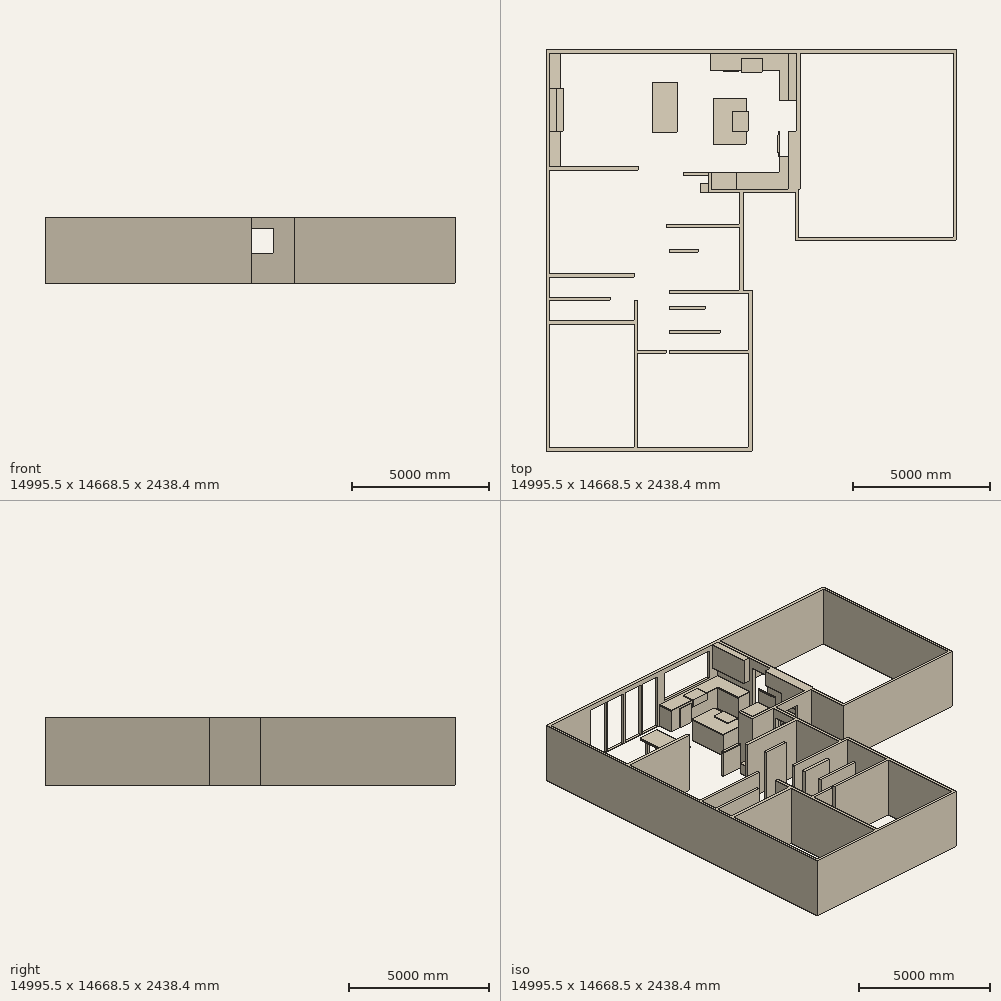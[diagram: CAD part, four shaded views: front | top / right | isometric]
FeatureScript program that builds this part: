
annotation { "Feature Type Name" : "Feature", "Feature Type Description" : "" }
export const myFeature = defineFeature(function(context is Context, id is Id, definition is map)
    precondition{}
    {
        {
            var Q0;
            Q0=qCreatedBy(makeId("Top.planeOp"),FACE);
            var sketch = newSketch(context, id + "F0", { "sketchPlane" : qUnion([Q0])});
            skLineSegment(sketch, "E0.bottom", {"start": v(9277.35, -5108.57) * mm, "end": v(9156.7, -5108.57) * mm});
            skLineSegment(sketch, "E0.top", {"start": v(9277.35, -120.65) * mm, "end": v(9156.7, -120.65) * mm});
            skLineSegment(sketch, "E0.left", {"start": v(9277.35, -5108.57) * mm, "end": v(9277.35, -120.65) * mm});
            skLineSegment(sketch, "E0.right", {"start": v(9156.7, -5108.57) * mm, "end": v(9156.7, -120.65) * mm});
            skLineSegment(sketch, "E1.bottom", {"start": v(7067.55, -5108.57) * mm, "end": v(4381.5, -5108.57) * mm});
            skLineSegment(sketch, "E1.top", {"start": v(7067.55, -5229.22) * mm, "end": v(4381.5, -5229.23) * mm});
            skLineSegment(sketch, "E1.left", {"start": v(7067.55, -5108.57) * mm, "end": v(7067.55, -5229.22) * mm});
            skLineSegment(sketch, "E1.right", {"start": v(4381.5, -5108.57) * mm, "end": v(4381.5, -5229.23) * mm});
            skLineSegment(sketch, "E2.bottom", {"start": v(5921.37, -5108.57) * mm, "end": v(6042.03, -5108.57) * mm});
            skLineSegment(sketch, "E2.top", {"start": v(5921.37, -1587.5) * mm, "end": v(6042.03, -1587.5) * mm});
            skLineSegment(sketch, "E2.left", {"start": v(5921.38, -5108.57) * mm, "end": v(5921.37, -1587.5) * mm});
            skLineSegment(sketch, "E2.right", {"start": v(6042.03, -5108.57) * mm, "end": v(6042.02, -1587.5) * mm});
            skLineSegment(sketch, "E3.bottom", {"start": v(4381.5, -5108.57) * mm, "end": v(4502.15, -5108.57) * mm});
            skLineSegment(sketch, "E3.top", {"start": v(4381.5, -4279.9) * mm, "end": v(4502.15, -4279.9) * mm});
            skLineSegment(sketch, "E3.left", {"start": v(4381.5, -5108.57) * mm, "end": v(4381.5, -4279.9) * mm});
            skLineSegment(sketch, "E3.right", {"start": v(4502.15, -5108.57) * mm, "end": v(4502.15, -4279.9) * mm});
            skLineSegment(sketch, "E4.bottom", {"start": v(4502.15, -4279.9) * mm, "end": v(5921.37, -4279.9) * mm});
            skLineSegment(sketch, "E4.top", {"start": v(4502.15, -4400.55) * mm, "end": v(5921.38, -4400.55) * mm});
            skLineSegment(sketch, "E4.left", {"start": v(4502.15, -4279.9) * mm, "end": v(4502.15, -4400.55) * mm});
            skLineSegment(sketch, "E4.right", {"start": v(5921.38, -4279.9) * mm, "end": v(5921.38, -4400.55) * mm});
            skLineSegment(sketch, "E5.bottom", {"start": v(120.65, -4279.9) * mm, "end": v(3346.45, -4279.9) * mm});
            skLineSegment(sketch, "E5.top", {"start": v(120.65, -4400.55) * mm, "end": v(3346.45, -4400.55) * mm});
            skLineSegment(sketch, "E5.left", {"start": v(120.65, -4279.9) * mm, "end": v(120.65, -4400.55) * mm});
            skLineSegment(sketch, "E5.right", {"start": v(3346.45, -4279.9) * mm, "end": v(3346.45, -4400.55) * mm});
            skLineSegment(sketch, "E6.bottom", {"start": v(3346.45, -4400.55) * mm, "end": v(3225.8, -4400.55) * mm});
            skLineSegment(sketch, "E6.top", {"start": v(3346.45, -9169.4) * mm, "end": v(3225.8, -9169.4) * mm});
            skLineSegment(sketch, "E6.left", {"start": v(3346.45, -4400.55) * mm, "end": v(3346.45, -9169.4) * mm});
            skLineSegment(sketch, "E6.right", {"start": v(3225.8, -4400.55) * mm, "end": v(3225.8, -9169.4) * mm});
            skLineSegment(sketch, "E7.bottom", {"start": v(2343.15, -9169.4) * mm, "end": v(120.65, -9169.4) * mm});
            skLineSegment(sketch, "E7.top", {"start": v(2343.15, -9048.75) * mm, "end": v(120.65, -9048.75) * mm});
            skLineSegment(sketch, "E7.left", {"start": v(3225.8, -9169.4) * mm, "end": v(3225.8, -9048.75) * mm});
            skLineSegment(sketch, "E7.right", {"start": v(120.65, -9169.4) * mm, "end": v(120.65, -9048.75) * mm});
            skLineSegment(sketch, "E8.bottom", {"start": v(3225.8, -8191.5) * mm, "end": v(120.65, -8191.5) * mm});
            skLineSegment(sketch, "E8.top", {"start": v(3225.8, -8312.15) * mm, "end": v(120.65, -8312.15) * mm});
            skLineSegment(sketch, "E8.left", {"start": v(3225.8, -8191.5) * mm, "end": v(3225.8, -8312.15) * mm});
            skLineSegment(sketch, "E8.right", {"start": v(120.65, -8191.5) * mm, "end": v(120.65, -8312.15) * mm});
            skLineSegment(sketch, "E9.bottom", {"start": v(7067.55, -6486.53) * mm, "end": v(4381.5, -6486.53) * mm});
            skLineSegment(sketch, "E9.top", {"start": v(7067.55, -6365.87) * mm, "end": v(4381.5, -6365.88) * mm});
            skLineSegment(sketch, "E9.left", {"start": v(7067.55, -6486.53) * mm, "end": v(7067.55, -6365.87) * mm});
            skLineSegment(sketch, "E9.right", {"start": v(4381.5, -6486.53) * mm, "end": v(4381.5, -6365.88) * mm});
            skLineSegment(sketch, "E10.bottom", {"start": v(4381.5, -6486.53) * mm, "end": v(4502.15, -6486.53) * mm});
            skLineSegment(sketch, "E10.top", {"start": v(4381.5, -11118.85) * mm, "end": v(4502.15, -11118.85) * mm});
            skLineSegment(sketch, "E10.left", {"start": v(4381.5, -6486.53) * mm, "end": v(4381.5, -11118.85) * mm});
            skLineSegment(sketch, "E10.right", {"start": v(4502.15, -6486.53) * mm, "end": v(4502.15, -11118.85) * mm});
            skLineSegment(sketch, "E11.bottom", {"start": v(4502.15, -8791.57) * mm, "end": v(7067.55, -8791.57) * mm});
            skLineSegment(sketch, "E11.top", {"start": v(4502.15, -8912.22) * mm, "end": v(7067.55, -8912.22) * mm});
            skLineSegment(sketch, "E11.left", {"start": v(4502.15, -8791.57) * mm, "end": v(4502.15, -8912.22) * mm});
            skLineSegment(sketch, "E11.right", {"start": v(7067.55, -8791.57) * mm, "end": v(7067.55, -8912.22) * mm});
            skLineSegment(sketch, "E12.bottom", {"start": v(4502.15, -11118.85) * mm, "end": v(7397.75, -11118.85) * mm});
            skLineSegment(sketch, "E12.top", {"start": v(4502.15, -10998.2) * mm, "end": v(7397.75, -10998.2) * mm});
            skLineSegment(sketch, "E12.left", {"start": v(4502.15, -11118.85) * mm, "end": v(4502.15, -10998.2) * mm});
            skLineSegment(sketch, "E12.right", {"start": v(7397.75, -11118.85) * mm, "end": v(7397.75, -10998.2) * mm});
            skLineSegment(sketch, "E13.top", {"start": v(3346.45, -14547.85) * mm, "end": v(3225.8, -14547.85) * mm});
            skLineSegment(sketch, "E13.left", {"start": v(3346.45, -9169.4) * mm, "end": v(3346.45, -14547.85) * mm});
            skLineSegment(sketch, "E13.right", {"start": v(3225.8, -9169.4) * mm, "end": v(3225.8, -14547.85) * mm});
            skLineSegment(sketch, "E14.bottom", {"start": v(3225.8, -10026.65) * mm, "end": v(120.65, -10026.65) * mm});
            skLineSegment(sketch, "E14.top", {"start": v(3225.8, -9906) * mm, "end": v(120.65, -9906) * mm});
            skLineSegment(sketch, "E14.left", {"start": v(3225.8, -10026.65) * mm, "end": v(3225.8, -9906) * mm});
            skLineSegment(sketch, "E14.right", {"start": v(120.65, -10026.65) * mm, "end": v(120.65, -9906) * mm});
            skLineSegment(sketch, "E15.bottom", {"start": v(4381.5, -11118.85) * mm, "end": v(3346.45, -11118.85) * mm});
            skLineSegment(sketch, "E15.top", {"start": v(4381.5, -10998.2) * mm, "end": v(3346.45, -10998.2) * mm});
            skLineSegment(sketch, "E15.left", {"start": v(4381.5, -11118.85) * mm, "end": v(4381.5, -10998.2) * mm});
            skLineSegment(sketch, "E15.right", {"start": v(3346.45, -11118.85) * mm, "end": v(3346.45, -10998.2) * mm});
            skLineSegment(sketch, "E16.bottom", {"start": v(4502.15, -10363.2) * mm, "end": v(6369.05, -10363.2) * mm});
            skLineSegment(sketch, "E16.top", {"start": v(4502.15, -10242.55) * mm, "end": v(6369.05, -10242.55) * mm});
            skLineSegment(sketch, "E16.left", {"start": v(4502.15, -10363.2) * mm, "end": v(4502.15, -10242.55) * mm});
            skLineSegment(sketch, "E16.right", {"start": v(6369.05, -10363.2) * mm, "end": v(6369.05, -10242.55) * mm});
            skLineSegment(sketch, "E17.bottom", {"start": v(6369.05, -10363.2) * mm, "end": v(6248.4, -10363.2) * mm});
            skLineSegment(sketch, "E17.top", {"start": v(6369.05, -10998.2) * mm, "end": v(6248.4, -10998.2) * mm});
            skLineSegment(sketch, "E17.left", {"start": v(6369.05, -10363.2) * mm, "end": v(6369.05, -10998.2) * mm});
            skLineSegment(sketch, "E17.right", {"start": v(6248.4, -10363.2) * mm, "end": v(6248.4, -10998.2) * mm});
            skLineSegment(sketch, "E18.bottom", {"start": v(2343.15, -8312.15) * mm, "end": v(2463.8, -8312.15) * mm});
            skLineSegment(sketch, "E18.top", {"start": v(2343.15, -9906) * mm, "end": v(2463.8, -9906) * mm});
            skLineSegment(sketch, "E18.left", {"start": v(2343.15, -8312.15) * mm, "end": v(2343.15, -9906) * mm});
            skLineSegment(sketch, "E18.right", {"start": v(2463.8, -8312.15) * mm, "end": v(2463.8, -9906) * mm});
            skLineSegment(sketch, "E19.bottom", {"start": v(4502.15, -7419.98) * mm, "end": v(5562.6, -7419.98) * mm});
            skLineSegment(sketch, "E19.top", {"start": v(4502.15, -7299.33) * mm, "end": v(5562.6, -7299.33) * mm});
            skLineSegment(sketch, "E19.left", {"start": v(4502.15, -7419.98) * mm, "end": v(4502.15, -7299.33) * mm});
            skLineSegment(sketch, "E19.right", {"start": v(5562.6, -7419.98) * mm, "end": v(5562.6, -7299.33) * mm});
            skLineSegment(sketch, "E20.bottom", {"start": v(5562.6, -7299.33) * mm, "end": v(5441.95, -7299.33) * mm});
            skLineSegment(sketch, "E20.top", {"start": v(5562.6, -6486.53) * mm, "end": v(5441.95, -6486.53) * mm});
            skLineSegment(sketch, "E20.left", {"start": v(5562.6, -7299.33) * mm, "end": v(5562.6, -6486.53) * mm});
            skLineSegment(sketch, "E20.right", {"start": v(5441.95, -7299.33) * mm, "end": v(5441.95, -6486.53) * mm});
            skLineSegment(sketch, "E21.bottom", {"start": v(4502.15, -9369.42) * mm, "end": v(5816.6, -9369.42) * mm});
            skLineSegment(sketch, "E21.top", {"start": v(4502.15, -9490.07) * mm, "end": v(5816.6, -9490.07) * mm});
            skLineSegment(sketch, "E21.left", {"start": v(4502.15, -9369.42) * mm, "end": v(4502.15, -9490.07) * mm});
            skLineSegment(sketch, "E21.right", {"start": v(5816.6, -9369.42) * mm, "end": v(5816.6, -9490.07) * mm});
            skLineSegment(sketch, "E22.bottom", {"start": v(5816.6, -9369.42) * mm, "end": v(5695.95, -9369.42) * mm});
            skLineSegment(sketch, "E22.top", {"start": v(5816.6, -8912.22) * mm, "end": v(5695.95, -8912.22) * mm});
            skLineSegment(sketch, "E22.left", {"start": v(5816.6, -9369.42) * mm, "end": v(5816.6, -8912.22) * mm});
            skLineSegment(sketch, "E22.right", {"start": v(5695.95, -9369.42) * mm, "end": v(5695.95, -8912.22) * mm});
            skLineSegment(sketch, "E23", {"start": v(0, 0) * mm, "end": v(0, -14668.5) * mm});
            skLineSegment(sketch, "E24", {"start": v(0, -14668.5) * mm, "end": v(7518.4, -14668.5) * mm});
            skLineSegment(sketch, "E25", {"start": v(7518.4, -14668.5) * mm, "end": v(7518.4, -8791.57) * mm});
            skLineSegment(sketch, "E26", {"start": v(7188.2, -8791.57) * mm, "end": v(7518.4, -8791.57) * mm});
            skLineSegment(sketch, "E27", {"start": v(7188.2, -8791.57) * mm, "end": v(7188.2, -5229.22) * mm});
            skLineSegment(sketch, "E28", {"start": v(7188.2, -5229.22) * mm, "end": v(9099.55, -5229.22) * mm});
            skLineSegment(sketch, "E29", {"start": v(9099.55, -5229.22) * mm, "end": v(9099.55, -6985) * mm});
            skLineSegment(sketch, "E30", {"start": v(9099.55, -6985) * mm, "end": v(14995.53, -6985) * mm});
            skLineSegment(sketch, "E31", {"start": v(14995.53, -6985) * mm, "end": v(14995.53, 0) * mm});
            skLineSegment(sketch, "E32", {"start": v(14995.53, 0) * mm, "end": v(0, 0) * mm});
            skLineSegment(sketch, "E33.0", {"start": v(14874.88, -6864.35) * mm, "end": v(14874.88, -120.65) * mm});
            skLineSegment(sketch, "E33.1", {"start": v(9220.2, -6864.35) * mm, "end": v(14874.88, -6864.35) * mm});
            skLineSegment(sketch, "E33.2", {"start": v(14874.88, -120.65) * mm, "end": v(120.65, -120.65) * mm});
            skLineSegment(sketch, "E33.3", {"start": v(9220.2, -5108.57) * mm, "end": v(9220.2, -6864.35) * mm});
            skLineSegment(sketch, "E33.4", {"start": v(7067.55, -5108.57) * mm, "end": v(9220.2, -5108.57) * mm});
            skLineSegment(sketch, "E33.5", {"start": v(7067.55, -8912.22) * mm, "end": v(7067.55, -5108.57) * mm});
            skLineSegment(sketch, "E33.6", {"start": v(120.65, -120.65) * mm, "end": v(120.65, -14547.85) * mm});
            skLineSegment(sketch, "E33.7", {"start": v(120.65, -14547.85) * mm, "end": v(7397.75, -14547.85) * mm});
            skLineSegment(sketch, "E33.8", {"start": v(7397.75, -14547.85) * mm, "end": v(7397.75, -8912.22) * mm});
            skLineSegment(sketch, "E34", {"start": v(7397.75, -8912.22) * mm, "end": v(7067.55, -8912.22) * mm});
            skLineSegment(sketch, "E35", {"start": v(5921.38, -2908.3) * mm, "end": v(6042.03, -2908.3) * mm});
            skSolve(sketch);
        }
        {
            var Q0;
            Q0=makeQuery(id+"F0.imprint","IMPRINT",FACE,{"disambiguationData":[TD([[makeQuery(id+"F0.imprint","IMPRINT",EDGE,{"derivedFrom":sQuery(id+"F0.wireOp",EDGE,"E23")}),1.0]])]});
            var Q1;
            {var subQ3=sQuery(id+"F0.wireOp",EDGE,"E0.bottom");Q1=makeQuery(id+"F0.imprint","IMPRINT",FACE,{"disambiguationData":[TD([[makeQuery(id+"F0.imprint","IMPRINT",EDGE,{"derivedFrom":subQ3}),-1.0]])]});}
            var Q2;
            {var subQ0=sQuery(id+"F0.wireOp",EDGE,"E1.top");Q2=makeQuery(id+"F0.imprint","IMPRINT",FACE,{"disambiguationData":[TD([[makeQuery(id+"F0.imprint","IMPRINT",EDGE,{"derivedFrom":subQ0}),-1.0]])]});}
            var Q3;
            Q3=makeQuery(id+"F0.imprint","IMPRINT",FACE,{"disambiguationData":[TD([[makeQuery(id+"F0.imprint","IMPRINT",EDGE,{"derivedFrom":sQuery(id+"F0.wireOp",EDGE,"E3.bottom")}),1.0]])]});
            var Q4;
            Q4=makeQuery(id+"F0.imprint","IMPRINT",FACE,{"disambiguationData":[TD([[makeQuery(id+"F0.imprint","IMPRINT",EDGE,{"derivedFrom":sQuery(id+"F0.wireOp",EDGE,"E4.bottom")}),-1.0]])]});
            var Q5;
            {var subQ3=sQuery(id+"F0.wireOp",EDGE,"E2.bottom");Q5=makeQuery(id+"F0.imprint","IMPRINT",FACE,{"disambiguationData":[TD([[makeQuery(id+"F0.imprint","IMPRINT",EDGE,{"derivedFrom":subQ3}),1.0]])]});}
            var Q6;
            {var subQ1=sQuery(id+"F0.wireOp",EDGE,"E5.bottom");Q6=makeQuery(id+"F0.imprint","IMPRINT",FACE,{"disambiguationData":[TD([[makeQuery(id+"F0.imprint","IMPRINT",EDGE,{"derivedFrom":subQ1}),-1.0]])]});}
            var Q7;
            {var subQ3=sQuery(id+"F0.wireOp",EDGE,"E6.bottom");Q7=makeQuery(id+"F0.imprint","IMPRINT",FACE,{"disambiguationData":[TD([[makeQuery(id+"F0.imprint","IMPRINT",EDGE,{"derivedFrom":subQ3}),1.0]])]});}
            var Q8;
            {var subQ5=sQuery(id+"F0.wireOp",EDGE,"E8.bottom");Q8=makeQuery(id+"F0.imprint","IMPRINT",FACE,{"disambiguationData":[TD([[makeQuery(id+"F0.imprint","IMPRINT",EDGE,{"derivedFrom":subQ5}),1.0]])]});}
            var Q9;
            {var subQ3=sQuery(id+"F0.wireOp",EDGE,"E18.bottom");Q9=makeQuery(id+"F0.imprint","IMPRINT",FACE,{"disambiguationData":[TD([[makeQuery(id+"F0.imprint","IMPRINT",EDGE,{"derivedFrom":subQ3}),-1.0]])]});}
            var Q10;
            {var subQ0=sQuery(id+"F0.wireOp",EDGE,"E7.bottom");Q10=makeQuery(id+"F0.imprint","IMPRINT",FACE,{"disambiguationData":[TD([[makeQuery(id+"F0.imprint","IMPRINT",EDGE,{"derivedFrom":subQ0}),-1.0]])]});}
            var Q11;
            {var subQ1=sQuery(id+"F0.wireOp",EDGE,"E6.top");Q11=makeQuery(id+"F0.imprint","IMPRINT",FACE,{"disambiguationData":[TD([[makeQuery(id+"F0.imprint","IMPRINT",EDGE,{"derivedFrom":subQ1}),1.0]])]});}
            var Q12;
            {var subQ5=sQuery(id+"F0.wireOp",EDGE,"E14.bottom");Q12=makeQuery(id+"F0.imprint","IMPRINT",FACE,{"disambiguationData":[TD([[makeQuery(id+"F0.imprint","IMPRINT",EDGE,{"derivedFrom":subQ5}),-1.0]])]});}
            var Q13;
            {var subQ6=sQuery(id+"F0.wireOp",EDGE,"E10.bottom");Q13=makeQuery(id+"F0.imprint","IMPRINT",FACE,{"disambiguationData":[TD([[makeQuery(id+"F0.imprint","IMPRINT",EDGE,{"derivedFrom":subQ6}),-1.0]])]});}
            var Q14;
            Q14=makeQuery(id+"F0.imprint","IMPRINT",FACE,{"disambiguationData":[TD([[makeQuery(id+"F0.imprint","IMPRINT",EDGE,{"derivedFrom":sQuery(id+"F0.wireOp",EDGE,"E21.bottom")}),-1.0]])]});
            var Q15;
            Q15=makeQuery(id+"F0.imprint","IMPRINT",FACE,{"disambiguationData":[TD([[makeQuery(id+"F0.imprint","IMPRINT",EDGE,{"derivedFrom":sQuery(id+"F0.wireOp",EDGE,"E16.bottom")}),1.0]])]});
            var Q16;
            {var subQ5=sQuery(id+"F0.wireOp",EDGE,"E11.bottom");Q16=makeQuery(id+"F0.imprint","IMPRINT",FACE,{"disambiguationData":[TD([[makeQuery(id+"F0.imprint","IMPRINT",EDGE,{"derivedFrom":subQ5}),-1.0]])]});}
            var Q17;
            Q17=makeQuery(id+"F0.imprint","IMPRINT",FACE,{"disambiguationData":[TD([[makeQuery(id+"F0.imprint","IMPRINT",EDGE,{"derivedFrom":sQuery(id+"F0.wireOp",EDGE,"E22.bottom")}),-1.0]])]});
            var Q18;
            Q18=makeQuery(id+"F0.imprint","IMPRINT",FACE,{"disambiguationData":[TD([[makeQuery(id+"F0.imprint","IMPRINT",EDGE,{"derivedFrom":sQuery(id+"F0.wireOp",EDGE,"E17.bottom")}),1.0]])]});
            var Q19;
            {var subQ1=sQuery(id+"F0.wireOp",EDGE,"E9.top");Q19=makeQuery(id+"F0.imprint","IMPRINT",FACE,{"disambiguationData":[TD([[makeQuery(id+"F0.imprint","IMPRINT",EDGE,{"derivedFrom":subQ1}),1.0]])]});}
            var Q20;
            Q20=makeQuery(id+"F0.imprint","IMPRINT",FACE,{"disambiguationData":[TD([[makeQuery(id+"F0.imprint","IMPRINT",EDGE,{"derivedFrom":sQuery(id+"F0.wireOp",EDGE,"E20.bottom")}),-1.0]])]});
            var Q21;
            Q21=makeQuery(id+"F0.imprint","IMPRINT",FACE,{"disambiguationData":[TD([[makeQuery(id+"F0.imprint","IMPRINT",EDGE,{"derivedFrom":sQuery(id+"F0.wireOp",EDGE,"E19.bottom")}),1.0]])]});
            var Q22;
            {var subQ5=sQuery(id+"F0.wireOp",EDGE,"E12.bottom");Q22=makeQuery(id+"F0.imprint","IMPRINT",FACE,{"disambiguationData":[TD([[makeQuery(id+"F0.imprint","IMPRINT",EDGE,{"derivedFrom":subQ5}),1.0]])]});}
            var Q23;
            Q23=makeQuery(id+"F0.imprint","IMPRINT",FACE,{"disambiguationData":[TD([[makeQuery(id+"F0.imprint","IMPRINT",EDGE,{"derivedFrom":sQuery(id+"F0.wireOp",EDGE,"E15.bottom")}),-1.0]])]});
            extrude(context, id + "F1", {"entities" : qUnion([Q0, Q1, Q2, Q3, Q4, Q5, Q6, Q7, Q8, Q9, Q10, Q11, Q12, Q13, Q14, Q15, Q16, Q17, Q18, Q19, Q20, Q21, Q22, Q23]), "depth" : 2425.7 * mm});
        }
        {
            var Q0;
            {var subQ0=sQuery(id+"F0.wireOp",EDGE,"E33.2");Q0=makeQuery(id+"F1.opExtrude","SWEPT_FACE",FACE,{"disambiguationData":[OSD([subQ0]),TDD([makeQuery(id+"F0.imprint","IMPRINT",EDGE,{"disambiguationData":[TD([[makeQuery(id+"F0.imprint","INTERSECT",VERTEX,{"derivedFrom":[sQuery(id+"F0.wireOp",EDGE,"E0.right"),subQ0]}),-1.0]])],"derivedFrom":subQ0})])]});}
            var sketch = newSketch(context, id + "F2", { "sketchPlane" : qUnion([Q0])});
            skLineSegment(sketch, "E36.bottom", {"start": v(8699.5, 1016) * mm, "end": v(6261.1, 1016) * mm});
            skLineSegment(sketch, "E36.top", {"start": v(8699.5, 2222.5) * mm, "end": v(6261.1, 2222.5) * mm});
            skLineSegment(sketch, "E36.left", {"start": v(8699.5, 1016) * mm, "end": v(8699.5, 2222.5) * mm});
            skLineSegment(sketch, "E36.right", {"start": v(6261.1, 1016) * mm, "end": v(6261.1, 2222.5) * mm});
            skSolve(sketch);
        }
        {
            var Q0;
            {var subQ0=sQuery(id+"F2.wireOp",EDGE,"E36.left");Q0=makeQuery(id+"F2.imprint","IMPRINT",FACE,{"disambiguationData":[TD([[makeQuery(id+"F2.imprint","IMPRINT",EDGE,{"derivedFrom":subQ0}),1.0]])]});}
            var Q1;
            {var subQ0=sQuery(id+"F2.wireOp",EDGE,"E36.right");Q1=makeQuery(id+"F2.imprint","IMPRINT",FACE,{"disambiguationData":[TD([[makeQuery(id+"F2.imprint","IMPRINT",EDGE,{"derivedFrom":subQ0}),-1.0]])]});}
            var Q2;
            Q2=makeQuery(id+"F2.imprint","IMPRINT",FACE,{"disambiguationData":[TD([[makeQuery(id+"F2.imprint","IMPRINT",EDGE,{"derivedFrom":sQuery(id+"F2.wireOp",EDGE,"sRTVKqyJ-7kPZ-i7xU-W92U-wSyeCJiGsMnf.bottom")}),1.0]])]});
            extrude(context, id + "F3", {"entities" : qUnion([Q0, Q1, Q2]), "operationType" : NewBodyOperationType.REMOVE, "endBound" : BoundingType.THROUGH_ALL, "oppositeDirection" : true, "depth" : 25.4 * mm});
        }
        {
            var Q0;
            Q0=makeQuery(id+"F1.opExtrude","SWEPT_FACE",FACE,{"disambiguationData":[OSD([sQuery(id+"F0.wireOp",EDGE,"E1.bottom"),sQuery(id+"F0.wireOp",EDGE,"E33.4")])]});
            var sketch = newSketch(context, id + "F4", { "sketchPlane" : qUnion([Q0])});
            skLineSegment(sketch, "E37.bottom", {"start": v(-8340.73, 2025.65) * mm, "end": v(-7432.68, 2025.65) * mm});
            skLineSegment(sketch, "E37.top", {"start": v(-8340.73, 1111.25) * mm, "end": v(-7432.68, 1111.25) * mm});
            skLineSegment(sketch, "E37.left", {"start": v(-8340.73, 2025.65) * mm, "end": v(-8340.73, 1111.25) * mm});
            skLineSegment(sketch, "E37.right", {"start": v(-7432.68, 2025.65) * mm, "end": v(-7432.68, 1111.25) * mm});
            skSolve(sketch);
        }
        {
            var Q0;
            Q0=makeQuery(id+"F4.imprint","IMPRINT",FACE,{"disambiguationData":[TD([[makeQuery(id+"F4.imprint","IMPRINT",EDGE,{"derivedFrom":sQuery(id+"F4.wireOp",EDGE,"E37.bottom")}),-1.0]])]});
            extrude(context, id + "F5", {"entities" : qUnion([Q0]), "operationType" : NewBodyOperationType.REMOVE, "endBound" : BoundingType.UP_TO_NEXT, "oppositeDirection" : true, "depth" : 25.4 * mm});
        }
        {
            var Q0;
            {var subQ0=sQuery(id+"F0.wireOp",EDGE,"E2.top");Q0=makeQuery(id+"F0.imprint","IMPRINT",FACE,{"disambiguationData":[TD([[makeQuery(id+"F0.imprint","IMPRINT",EDGE,{"derivedFrom":subQ0}),-1.0]])]});}
            extrude(context, id + "F6", {"entities" : qUnion([Q0]), "operationType" : NewBodyOperationType.ADD, "depth" : 914.4 * mm});
        }
        {
            var Q0;
            Q0=makeQuery(id+"F1.opExtrude","SWEPT_FACE",FACE,{"disambiguationData":[OSD([sQuery(id+"F0.wireOp",EDGE,"E0.right")])]});
            var sketch = newSketch(context, id + "F7", { "sketchPlane" : qUnion([Q0])});
            skLineSegment(sketch, "E38.bottom", {"start": v(2006.6, 0) * mm, "end": v(2819.4, 0) * mm});
            skLineSegment(sketch, "E38.top", {"start": v(2006.6, 2032) * mm, "end": v(2819.4, 2032) * mm});
            skLineSegment(sketch, "E38.left", {"start": v(2006.6, 0) * mm, "end": v(2006.6, 2032) * mm});
            skLineSegment(sketch, "E38.right", {"start": v(2819.4, 0) * mm, "end": v(2819.4, 2032) * mm});
            skSolve(sketch);
        }
        {
            var Q0;
            Q0=makeQuery(id+"F7.imprint","IMPRINT",FACE,{"disambiguationData":[TD([[makeQuery(id+"F7.imprint","IMPRINT",EDGE,{"derivedFrom":sQuery(id+"F7.wireOp",EDGE,"E38.bottom")}),-1.0]])]});
            extrude(context, id + "F8", {"entities" : qUnion([Q0]), "operationType" : NewBodyOperationType.REMOVE, "endBound" : BoundingType.UP_TO_NEXT, "oppositeDirection" : true, "depth" : 25.4 * mm});
        }
        {
            var Q0;
            {var subQ0=sQuery(id+"F0.wireOp",EDGE,"E33.2");Q0=makeQuery(id+"F1.opExtrude","SWEPT_FACE",FACE,{"disambiguationData":[OSD([subQ0]),TDD([makeQuery(id+"F0.imprint","IMPRINT",EDGE,{"disambiguationData":[TD([[makeQuery(id+"F0.imprint","INTERSECT",VERTEX,{"derivedFrom":[sQuery(id+"F0.wireOp",EDGE,"E0.right"),subQ0]}),-1.0]])],"derivedFrom":subQ0})])]});}
            var sketch = newSketch(context, id + "F9", { "sketchPlane" : qUnion([Q0])});
            skLineSegment(sketch, "E39.bottom", {"start": v(2254.25, 25.4) * mm, "end": v(3117.85, 25.4) * mm});
            skLineSegment(sketch, "E39.top", {"start": v(2254.25, 2222.5) * mm, "end": v(3117.85, 2222.5) * mm});
            skLineSegment(sketch, "E39.left", {"start": v(2254.25, 25.4) * mm, "end": v(2254.25, 2222.5) * mm});
            skLineSegment(sketch, "E39.right", {"start": v(3117.85, 25.4) * mm, "end": v(3117.85, 2222.5) * mm});
            skLineSegment(sketch, "E40.bottom", {"start": v(3168.65, 25.4) * mm, "end": v(4032.25, 25.4) * mm});
            skLineSegment(sketch, "E40.top", {"start": v(3168.65, 2222.5) * mm, "end": v(4032.25, 2222.5) * mm});
            skLineSegment(sketch, "E40.left", {"start": v(3168.65, 25.4) * mm, "end": v(3168.65, 2222.5) * mm});
            skLineSegment(sketch, "E40.right", {"start": v(4032.25, 25.4) * mm, "end": v(4032.25, 2222.5) * mm});
            skLineSegment(sketch, "E41.bottom", {"start": v(4133.85, 25.4) * mm, "end": v(4997.45, 25.4) * mm});
            skLineSegment(sketch, "E41.top", {"start": v(4133.85, 2222.5) * mm, "end": v(4997.45, 2222.5) * mm});
            skLineSegment(sketch, "E41.left", {"start": v(4133.85, 25.4) * mm, "end": v(4133.85, 2222.5) * mm});
            skLineSegment(sketch, "E41.right", {"start": v(4997.45, 25.4) * mm, "end": v(4997.45, 2222.5) * mm});
            skLineSegment(sketch, "E42.bottom", {"start": v(5048.25, 25.4) * mm, "end": v(5911.85, 25.4) * mm});
            skLineSegment(sketch, "E42.top", {"start": v(5048.25, 2222.5) * mm, "end": v(5911.85, 2222.5) * mm});
            skLineSegment(sketch, "E42.left", {"start": v(5048.25, 25.4) * mm, "end": v(5048.25, 2222.5) * mm});
            skLineSegment(sketch, "E42.right", {"start": v(5911.85, 25.4) * mm, "end": v(5911.85, 2222.5) * mm});
            skSolve(sketch);
        }
        {
            var Q0;
            Q0=makeQuery(id+"F9.imprint","IMPRINT",FACE,{"disambiguationData":[TD([[makeQuery(id+"F9.imprint","IMPRINT",EDGE,{"derivedFrom":sQuery(id+"F9.wireOp",EDGE,"E39.bottom")}),1.0]])]});
            var Q1;
            Q1=makeQuery(id+"F9.imprint","IMPRINT",FACE,{"disambiguationData":[TD([[makeQuery(id+"F9.imprint","IMPRINT",EDGE,{"derivedFrom":sQuery(id+"F9.wireOp",EDGE,"E40.bottom")}),1.0]])]});
            var Q2;
            Q2=makeQuery(id+"F9.imprint","IMPRINT",FACE,{"disambiguationData":[TD([[makeQuery(id+"F9.imprint","IMPRINT",EDGE,{"derivedFrom":sQuery(id+"F9.wireOp",EDGE,"E41.bottom")}),1.0]])]});
            var Q3;
            Q3=makeQuery(id+"F9.imprint","IMPRINT",FACE,{"disambiguationData":[TD([[makeQuery(id+"F9.imprint","IMPRINT",EDGE,{"derivedFrom":sQuery(id+"F9.wireOp",EDGE,"E42.bottom")}),1.0]])]});
            extrude(context, id + "F10", {"entities" : qUnion([Q0, Q1, Q2, Q3]), "operationType" : NewBodyOperationType.REMOVE, "endBound" : BoundingType.THROUGH_ALL, "oppositeDirection" : true, "depth" : 25.4 * mm});
        }
        {
            var Q0;
            {var subQ0=sQuery(id+"F0.wireOp",EDGE,"E33.5");Q0=makeQuery(id+"F1.opExtrude","SWEPT_FACE",FACE,{"disambiguationData":[OSD([subQ0]),TDD([makeQuery(id+"F0.imprint","IMPRINT",EDGE,{"disambiguationData":[TD([[makeQuery(id+"F0.imprint","INTERSECT",VERTEX,{"derivedFrom":[sQuery(id+"F0.wireOp",EDGE,"E1.top"),subQ0]}),1.0]])],"derivedFrom":subQ0})])]});}
            var sketch = newSketch(context, id + "F11", { "sketchPlane" : qUnion([Q0])});
            skLineSegment(sketch, "E43.bottom", {"start": v(5343.52, 0) * mm, "end": v(6248.4, 0) * mm});
            skLineSegment(sketch, "E43.top", {"start": v(5343.52, 2038.35) * mm, "end": v(6248.4, 2038.35) * mm});
            skLineSegment(sketch, "E43.left", {"start": v(5343.52, 0) * mm, "end": v(5343.52, 2038.35) * mm});
            skLineSegment(sketch, "E43.right", {"start": v(6248.4, 0) * mm, "end": v(6248.4, 2038.35) * mm});
            skSolve(sketch);
        }
        {
            var Q0;
            Q0=makeQuery(id+"F11.imprint","IMPRINT",FACE,{"disambiguationData":[TD([[makeQuery(id+"F11.imprint","IMPRINT",EDGE,{"derivedFrom":sQuery(id+"F11.wireOp",EDGE,"E43.bottom")}),-1.0]])]});
            extrude(context, id + "F12", {"entities" : qUnion([Q0]), "operationType" : NewBodyOperationType.REMOVE, "endBound" : BoundingType.UP_TO_NEXT, "oppositeDirection" : true, "depth" : 25.4 * mm});
        }
        {
            var Q0;
            Q0=makeQuery(id+"F1.opExtrude","CAP_FACE",FACE,{"disambiguationData":[OSD([sQuery(id+"F0.wireOp",EDGE,"E0.bottom"),sQuery(id+"F0.wireOp",EDGE,"E0.left"),sQuery(id+"F0.wireOp",EDGE,"E0.right"),sQuery(id+"F0.wireOp",EDGE,"E1.bottom"),sQuery(id+"F0.wireOp",EDGE,"E1.top"),sQuery(id+"F0.wireOp",EDGE,"E1.right"),sQuery(id+"F0.wireOp",EDGE,"E2.left"),sQuery(id+"F0.wireOp",EDGE,"E2.right"),sQuery(id+"F0.wireOp",EDGE,"E3.top"),sQuery(id+"F0.wireOp",EDGE,"E3.left"),sQuery(id+"F0.wireOp",EDGE,"E3.right"),sQuery(id+"F0.wireOp",EDGE,"E4.bottom"),sQuery(id+"F0.wireOp",EDGE,"E4.top"),sQuery(id+"F0.wireOp",EDGE,"E5.bottom"),sQuery(id+"F0.wireOp",EDGE,"E5.top"),sQuery(id+"F0.wireOp",EDGE,"E5.right"),sQuery(id+"F0.wireOp",EDGE,"E6.left"),sQuery(id+"F0.wireOp",EDGE,"E6.right"),sQuery(id+"F0.wireOp",EDGE,"E7.bottom"),sQuery(id+"F0.wireOp",EDGE,"E7.top"),sQuery(id+"F0.wireOp",EDGE,"E7.left"),sQuery(id+"F0.wireOp",EDGE,"E8.bottom"),sQuery(id+"F0.wireOp",EDGE,"E8.top"),sQuery(id+"F0.wireOp",EDGE,"E9.bottom"),sQuery(id+"F0.wireOp",EDGE,"E9.top"),sQuery(id+"F0.wireOp",EDGE,"E9.right"),sQuery(id+"F0.wireOp",EDGE,"E10.top"),sQuery(id+"F0.wireOp",EDGE,"E10.left"),sQuery(id+"F0.wireOp",EDGE,"E10.right"),sQuery(id+"F0.wireOp",EDGE,"E11.bottom"),sQuery(id+"F0.wireOp",EDGE,"E11.top"),sQuery(id+"F0.wireOp",EDGE,"E12.bottom"),sQuery(id+"F0.wireOp",EDGE,"E12.top"),sQuery(id+"F0.wireOp",EDGE,"E13.left"),sQuery(id+"F0.wireOp",EDGE,"E13.right"),sQuery(id+"F0.wireOp",EDGE,"E14.bottom"),sQuery(id+"F0.wireOp",EDGE,"E14.top"),sQuery(id+"F0.wireOp",EDGE,"E15.bottom"),sQuery(id+"F0.wireOp",EDGE,"E15.top"),sQuery(id+"F0.wireOp",EDGE,"E16.bottom"),sQuery(id+"F0.wireOp",EDGE,"E16.top"),sQuery(id+"F0.wireOp",EDGE,"E16.right"),sQuery(id+"F0.wireOp",EDGE,"E17.left"),sQuery(id+"F0.wireOp",EDGE,"E17.right"),sQuery(id+"F0.wireOp",EDGE,"E18.left"),sQuery(id+"F0.wireOp",EDGE,"E18.right"),sQuery(id+"F0.wireOp",EDGE,"E19.bottom"),sQuery(id+"F0.wireOp",EDGE,"E19.top"),sQuery(id+"F0.wireOp",EDGE,"E19.right"),sQuery(id+"F0.wireOp",EDGE,"E20.left"),sQuery(id+"F0.wireOp",EDGE,"E20.right"),sQuery(id+"F0.wireOp",EDGE,"E21.bottom"),sQuery(id+"F0.wireOp",EDGE,"E21.top"),sQuery(id+"F0.wireOp",EDGE,"E21.right"),sQuery(id+"F0.wireOp",EDGE,"E22.left"),sQuery(id+"F0.wireOp",EDGE,"E22.right"),sQuery(id+"F0.wireOp",EDGE,"E23"),sQuery(id+"F0.wireOp",EDGE,"E24"),sQuery(id+"F0.wireOp",EDGE,"E25"),sQuery(id+"F0.wireOp",EDGE,"E26"),sQuery(id+"F0.wireOp",EDGE,"E27"),sQuery(id+"F0.wireOp",EDGE,"E28"),sQuery(id+"F0.wireOp",EDGE,"E29"),sQuery(id+"F0.wireOp",EDGE,"E30"),sQuery(id+"F0.wireOp",EDGE,"E31"),sQuery(id+"F0.wireOp",EDGE,"E32"),sQuery(id+"F0.wireOp",EDGE,"E33.0"),sQuery(id+"F0.wireOp",EDGE,"E33.1"),sQuery(id+"F0.wireOp",EDGE,"E33.2"),sQuery(id+"F0.wireOp",EDGE,"E33.3"),sQuery(id+"F0.wireOp",EDGE,"E33.4"),sQuery(id+"F0.wireOp",EDGE,"E33.5"),sQuery(id+"F0.wireOp",EDGE,"E33.6"),sQuery(id+"F0.wireOp",EDGE,"E33.7"),sQuery(id+"F0.wireOp",EDGE,"E33.8"),sQuery(id+"F0.wireOp",EDGE,"E34"),sQuery(id+"F0.wireOp",EDGE,"E35")])],"isStart":false});
            var sketch = newSketch(context, id + "F13", { "sketchPlane" : qUnion([Q0])});
            skLineSegment(sketch, "E44.0", {"start": v(6051.55, -5229.22) * mm, "end": v(4381.5, -5229.23) * mm});
            skLineSegment(sketch, "E45.0", {"start": v(4381.5, -4279.9) * mm, "end": v(4381.5, -5229.23) * mm});
            skLineSegment(sketch, "E46.0", {"start": v(4381.5, -4279.9) * mm, "end": v(5921.38, -4279.9) * mm});
            skLineSegment(sketch, "E47.0", {"start": v(6042.03, -5108.57) * mm, "end": v(6042.02, -1587.5) * mm});
            skLineSegment(sketch, "E48.0", {"start": v(5921.38, -4279.9) * mm, "end": v(5921.37, -1587.5) * mm});
            skLineSegment(sketch, "E49.0", {"start": v(5921.37, -1587.5) * mm, "end": v(6042.02, -1587.5) * mm});
            skLineSegment(sketch, "E50", {"start": v(6051.55, -5108.57) * mm, "end": v(6042.03, -5108.57) * mm});
            skLineSegment(sketch, "E51", {"start": v(6051.55, -5108.57) * mm, "end": v(6051.55, -5229.22) * mm});
            skPoint(sketch, "E52.start.orphan", {"position": v(7067.55, -5229.22) * mm});
            skPoint(sketch, "E53.0.end.orphan", {"position": v(9156.7, -5108.57) * mm});
            skPoint(sketch, "E53.0.start.orphan", {"position": v(6042.03, -5108.57) * mm});
            skSolve(sketch);
        }
        {
            var Q0;
            Q0=makeQuery(id+"F13.imprint","IMPRINT",FACE,{"disambiguationData":[TD([[makeQuery(id+"F13.imprint","IMPRINT",EDGE,{"derivedFrom":sQuery(id+"F13.wireOp",EDGE,"E44.0")}),-1.0]])]});
            var Q1;
            {var subQ2=sQuery(id+"F13.wireOp",EDGE,"E49.0");Q1=makeQuery(id+"F13.imprint","IMPRINT",FACE,{"disambiguationData":[TD([[makeQuery(id+"F13.imprint","IMPRINT",EDGE,{"derivedFrom":subQ2}),-1.0]])]});}
            extrude(context, id + "F14", {"entities" : qUnion([Q0, Q1]), "operationType" : NewBodyOperationType.REMOVE, "endBound" : BoundingType.THROUGH_ALL, "oppositeDirection" : true, "depth" : 25.4 * mm});
        }
        {
            var Q0;
            Q0=makeQuery(id+"F1.opExtrude","CAP_FACE",FACE,{"disambiguationData":[OSD([sQuery(id+"F0.wireOp",EDGE,"E0.bottom"),sQuery(id+"F0.wireOp",EDGE,"E0.left"),sQuery(id+"F0.wireOp",EDGE,"E0.right"),sQuery(id+"F0.wireOp",EDGE,"E1.bottom"),sQuery(id+"F0.wireOp",EDGE,"E1.top"),sQuery(id+"F0.wireOp",EDGE,"E1.right"),sQuery(id+"F0.wireOp",EDGE,"E2.left"),sQuery(id+"F0.wireOp",EDGE,"E2.right"),sQuery(id+"F0.wireOp",EDGE,"E3.top"),sQuery(id+"F0.wireOp",EDGE,"E3.left"),sQuery(id+"F0.wireOp",EDGE,"E3.right"),sQuery(id+"F0.wireOp",EDGE,"E4.bottom"),sQuery(id+"F0.wireOp",EDGE,"E4.top"),sQuery(id+"F0.wireOp",EDGE,"E5.bottom"),sQuery(id+"F0.wireOp",EDGE,"E5.top"),sQuery(id+"F0.wireOp",EDGE,"E5.right"),sQuery(id+"F0.wireOp",EDGE,"E6.left"),sQuery(id+"F0.wireOp",EDGE,"E6.right"),sQuery(id+"F0.wireOp",EDGE,"E7.bottom"),sQuery(id+"F0.wireOp",EDGE,"E7.top"),sQuery(id+"F0.wireOp",EDGE,"E7.left"),sQuery(id+"F0.wireOp",EDGE,"E8.bottom"),sQuery(id+"F0.wireOp",EDGE,"E8.top"),sQuery(id+"F0.wireOp",EDGE,"E9.bottom"),sQuery(id+"F0.wireOp",EDGE,"E9.top"),sQuery(id+"F0.wireOp",EDGE,"E9.right"),sQuery(id+"F0.wireOp",EDGE,"E10.top"),sQuery(id+"F0.wireOp",EDGE,"E10.left"),sQuery(id+"F0.wireOp",EDGE,"E10.right"),sQuery(id+"F0.wireOp",EDGE,"E11.bottom"),sQuery(id+"F0.wireOp",EDGE,"E11.top"),sQuery(id+"F0.wireOp",EDGE,"E12.bottom"),sQuery(id+"F0.wireOp",EDGE,"E12.top"),sQuery(id+"F0.wireOp",EDGE,"E13.left"),sQuery(id+"F0.wireOp",EDGE,"E13.right"),sQuery(id+"F0.wireOp",EDGE,"E14.bottom"),sQuery(id+"F0.wireOp",EDGE,"E14.top"),sQuery(id+"F0.wireOp",EDGE,"E15.bottom"),sQuery(id+"F0.wireOp",EDGE,"E15.top"),sQuery(id+"F0.wireOp",EDGE,"E16.bottom"),sQuery(id+"F0.wireOp",EDGE,"E16.top"),sQuery(id+"F0.wireOp",EDGE,"E16.right"),sQuery(id+"F0.wireOp",EDGE,"E17.left"),sQuery(id+"F0.wireOp",EDGE,"E17.right"),sQuery(id+"F0.wireOp",EDGE,"E18.left"),sQuery(id+"F0.wireOp",EDGE,"E18.right"),sQuery(id+"F0.wireOp",EDGE,"E19.bottom"),sQuery(id+"F0.wireOp",EDGE,"E19.top"),sQuery(id+"F0.wireOp",EDGE,"E19.right"),sQuery(id+"F0.wireOp",EDGE,"E20.left"),sQuery(id+"F0.wireOp",EDGE,"E20.right"),sQuery(id+"F0.wireOp",EDGE,"E21.bottom"),sQuery(id+"F0.wireOp",EDGE,"E21.top"),sQuery(id+"F0.wireOp",EDGE,"E21.right"),sQuery(id+"F0.wireOp",EDGE,"E22.left"),sQuery(id+"F0.wireOp",EDGE,"E22.right"),sQuery(id+"F0.wireOp",EDGE,"E23"),sQuery(id+"F0.wireOp",EDGE,"E24"),sQuery(id+"F0.wireOp",EDGE,"E25"),sQuery(id+"F0.wireOp",EDGE,"E26"),sQuery(id+"F0.wireOp",EDGE,"E27"),sQuery(id+"F0.wireOp",EDGE,"E28"),sQuery(id+"F0.wireOp",EDGE,"E29"),sQuery(id+"F0.wireOp",EDGE,"E30"),sQuery(id+"F0.wireOp",EDGE,"E31"),sQuery(id+"F0.wireOp",EDGE,"E32"),sQuery(id+"F0.wireOp",EDGE,"E33.0"),sQuery(id+"F0.wireOp",EDGE,"E33.1"),sQuery(id+"F0.wireOp",EDGE,"E33.2"),sQuery(id+"F0.wireOp",EDGE,"E33.3"),sQuery(id+"F0.wireOp",EDGE,"E33.4"),sQuery(id+"F0.wireOp",EDGE,"E33.5"),sQuery(id+"F0.wireOp",EDGE,"E33.6"),sQuery(id+"F0.wireOp",EDGE,"E33.7"),sQuery(id+"F0.wireOp",EDGE,"E33.8"),sQuery(id+"F0.wireOp",EDGE,"E34"),sQuery(id+"F0.wireOp",EDGE,"E35")])],"isStart":false});
            var sketch = newSketch(context, id + "F15", { "sketchPlane" : qUnion([Q0])});
            skLineSegment(sketch, "E54.bottom", {"start": v(6051.55, -5229.22) * mm, "end": v(5924.55, -5229.22) * mm});
            skLineSegment(sketch, "E54.top", {"start": v(6051.55, -4467.22) * mm, "end": v(5924.55, -4467.22) * mm});
            skLineSegment(sketch, "E54.left", {"start": v(6051.55, -5229.22) * mm, "end": v(6051.55, -4467.22) * mm});
            skLineSegment(sketch, "E54.right", {"start": v(5924.55, -5229.22) * mm, "end": v(5924.55, -4467.22) * mm});
            skSolve(sketch);
        }
        {
            var Q0;
            {var subQ1=sQuery(id+"F15.wireOp",EDGE,"E54.bottom");Q0=makeQuery(id+"F15.imprint","IMPRINT",FACE,{"disambiguationData":[TD([[makeQuery(id+"F15.imprint","IMPRINT",EDGE,{"derivedFrom":subQ1}),-1.0]])]});}
            var Q1;
            {var subQ0=sQuery(id+"F0.wireOp",EDGE,"E22.right");var subQ2=sQuery(id+"F0.wireOp",EDGE,"E13.left");var subQ3=sQuery(id+"F0.wireOp",EDGE,"E6.left");var subQ4=sQuery(id+"F0.wireOp",EDGE,"E5.right");var subQ6=sQuery(id+"F0.wireOp",EDGE,"E21.top");var subQ8=sQuery(id+"F0.wireOp",EDGE,"E20.right");var subQ10=sQuery(id+"F0.wireOp",EDGE,"E20.left");var subQ11=sQuery(id+"F0.wireOp",EDGE,"E19.right");var subQ13=sQuery(id+"F0.wireOp",EDGE,"E33.5");var subQ14=sQuery(id+"F0.wireOp",EDGE,"E1.top");var subQ15=sQuery(id+"F0.wireOp",EDGE,"E9.top");var subQ17=sQuery(id+"F0.wireOp",EDGE,"E19.bottom");var subQ19=sQuery(id+"F0.wireOp",EDGE,"E18.left");var subQ20=sQuery(id+"F0.wireOp",EDGE,"E7.bottom");var subQ22=sQuery(id+"F0.wireOp",EDGE,"E14.top");var subQ25=sQuery(id+"F0.wireOp",EDGE,"E17.right");var subQ27=sQuery(id+"F0.wireOp",EDGE,"E33.6");var subQ28=sQuery(id+"F0.wireOp",EDGE,"E5.top");var subQ29=sQuery(id+"F0.wireOp",EDGE,"E8.bottom");var subQ31=sQuery(id+"F0.wireOp",EDGE,"E15.top");var subQ33=sQuery(id+"F0.wireOp",EDGE,"E19.top");var subQ35=sQuery(id+"F0.wireOp",EDGE,"E18.right");var subQ39=sQuery(id+"F0.wireOp",EDGE,"E13.right");var subQ41=sQuery(id+"F0.wireOp",EDGE,"E17.left");var subQ42=sQuery(id+"F0.wireOp",EDGE,"E16.right");var subQ45=sQuery(id+"F0.wireOp",EDGE,"E7.top");var subQ47=sQuery(id+"F0.wireOp",EDGE,"E8.top");var subQ50=sQuery(id+"F0.wireOp",EDGE,"E14.bottom");var subQ55=sQuery(id+"F0.wireOp",EDGE,"E9.bottom");var subQ57=sQuery(id+"F0.wireOp",EDGE,"E11.bottom");var subQ61=sQuery(id+"F0.wireOp",EDGE,"E5.bottom");var subQ62=makeQuery(id+"F1.opExtrude","SWEPT_FACE",FACE,{"disambiguationData":[OSD([subQ61])]});var subQ63=sQuery(id+"F0.wireOp",EDGE,"E21.bottom");var subQ66=sQuery(id+"F0.wireOp",EDGE,"E7.left");var subQ67=sQuery(id+"F0.wireOp",EDGE,"E6.right");var subQ69=sQuery(id+"F0.wireOp",EDGE,"E10.left");var subQ70=sQuery(id+"F0.wireOp",EDGE,"E9.right");var subQ73=sQuery(id+"F0.wireOp",EDGE,"E22.left");var subQ74=sQuery(id+"F0.wireOp",EDGE,"E21.right");var subQ77=sQuery(id+"F0.wireOp",EDGE,"E12.top");var subQ78=sQuery(id+"F0.wireOp",EDGE,"E10.right");var subQ81=sQuery(id+"F0.wireOp",EDGE,"E16.bottom");var subQ84=sQuery(id+"F0.wireOp",EDGE,"E11.top");var subQ91=sQuery(id+"F0.wireOp",EDGE,"E33.2");var subQ96=sQuery(id+"F0.wireOp",EDGE,"E16.top");var subQ99=sQuery(id+"F0.wireOp",EDGE,"E33.8");var subQ103=sQuery(id+"F0.wireOp",EDGE,"E34");var subQ106=sQuery(id+"F0.wireOp",EDGE,"E15.bottom");var subQ107=sQuery(id+"F0.wireOp",EDGE,"E12.bottom");var subQ108=sQuery(id+"F0.wireOp",EDGE,"E10.top");var subQ114=sQuery(id+"F0.wireOp",EDGE,"E33.7");var subQ123=sQuery(id+"F0.wireOp",EDGE,"E23");var subQ125=sQuery(id+"F0.wireOp",EDGE,"E24");var subQ127=sQuery(id+"F0.wireOp",EDGE,"E25");var subQ129=sQuery(id+"F0.wireOp",EDGE,"E26");var subQ131=sQuery(id+"F0.wireOp",EDGE,"E27");var subQ133=sQuery(id+"F0.wireOp",EDGE,"E32");var subQ135=sQuery(id+"F0.wireOp",EDGE,"E0.right");var subQ141=sQuery(id+"F0.wireOp",EDGE,"E2.right");var subQ142=sQuery(id+"F0.wireOp",EDGE,"E2.left");var subQ143=sQuery(id+"F0.wireOp",EDGE,"E1.bottom");var subQ145=sQuery(id+"F0.wireOp",EDGE,"E4.top");var subQ146=sQuery(id+"F0.wireOp",EDGE,"E3.left");var subQ147=sQuery(id+"F0.wireOp",EDGE,"E1.right");var subQ148=sQuery(id+"F0.wireOp",EDGE,"E33.1");var subQ149=sQuery(id+"F0.wireOp",EDGE,"E0.bottom");var subQ150=sQuery(id+"F0.wireOp",EDGE,"E4.bottom");var subQ151=sQuery(id+"F0.wireOp",EDGE,"E35");var subQ152=sQuery(id+"F0.wireOp",EDGE,"E0.left");var subQ153=sQuery(id+"F0.wireOp",EDGE,"E30");var subQ154=sQuery(id+"F0.wireOp",EDGE,"E33.4");var subQ155=sQuery(id+"F0.wireOp",EDGE,"E3.right");var subQ156=sQuery(id+"F0.wireOp",EDGE,"E3.top");var subQ157=sQuery(id+"F0.wireOp",EDGE,"E29");var subQ158=sQuery(id+"F0.wireOp",EDGE,"E28");var subQ159=sQuery(id+"F0.wireOp",EDGE,"E31");var subQ160=sQuery(id+"F0.wireOp",EDGE,"E33.0");var subQ161=sQuery(id+"F0.wireOp",EDGE,"E33.3");var subQ162=sQuery(id+"F0.wireOp",EDGE,"E2.top");Q1=makeQuery(id+"F12.boolean.opBoolean","SPLIT",FACE,{"disambiguationData":[TD([subQ62])],"derivedFrom":makeQuery(id+"F10.boolean.opBoolean","SPLIT",FACE,{"disambiguationData":[TD([makeQuery(id+"F1.opExtrude","SWEPT_FACE",FACE,{"disambiguationData":[OSD([subQ149])]})])],"derivedFrom":makeQuery(id+"F6.boolean.opBoolean","MERGE",FACE,{"derivedFrom":[makeQuery(id+"F1.opExtrude","CAP_FACE",FACE,{"disambiguationData":[OSD([subQ149,subQ152,subQ135,subQ143,subQ14,subQ147,subQ142,subQ141,subQ156,subQ146,subQ155,subQ150,subQ145,subQ61,subQ28,subQ4,subQ3,subQ67,subQ20,subQ45,subQ66,subQ29,subQ47,subQ55,subQ15,subQ70,subQ108,subQ69,subQ78,subQ57,subQ84,subQ107,subQ77,subQ2,subQ39,subQ50,subQ22,subQ106,subQ31,subQ81,subQ96,subQ42,subQ41,subQ25,subQ19,subQ35,subQ17,subQ33,subQ11,subQ10,subQ8,subQ63,subQ6,subQ74,subQ73,subQ0,subQ123,subQ125,subQ127,subQ129,subQ131,subQ158,subQ157,subQ153,subQ159,subQ133,subQ160,subQ148,subQ91,subQ161,subQ154,subQ13,subQ27,subQ114,subQ99,subQ103,subQ151])],"isStart":true}),makeQuery(id+"F6.opExtrude","CAP_FACE",FACE,{"disambiguationData":[OSD([subQ162,subQ142,subQ141,subQ151])],"isStart":true})]})})});}
            extrude(context, id + "F16", {"entities" : qUnion([Q0]), "operationType" : NewBodyOperationType.ADD, "endBound" : BoundingType.UP_TO_SURFACE, "oppositeDirection" : true, "endBoundEntityFace" : qUnion([Q1]), "depth" : 1530.35 * mm});
        }
        {
            var Q0;
            Q0=qCreatedBy(makeId("Top.planeOp"),FACE);
            var sketch = newSketch(context, id + "F17", { "sketchPlane" : qUnion([Q0])});
            skLineSegment(sketch, "E55.bottom", {"start": v(6051.55, -5108.57) * mm, "end": v(6051.55, -5108.57) * mm});
            skLineSegment(sketch, "E55.left", {"start": v(6051.55, -5108.57) * mm, "end": v(6051.55, -4473.57) * mm});
            skLineSegment(sketch, "E56.bottom", {"start": v(6051.55, -5108.57) * mm, "end": v(6965.95, -5108.57) * mm});
            skLineSegment(sketch, "E56.top", {"start": v(6051.55, -4473.57) * mm, "end": v(6965.95, -4473.57) * mm});
            skLineSegment(sketch, "E56.right", {"start": v(6965.95, -5108.57) * mm, "end": v(6965.95, -4473.57) * mm});
            skLineSegment(sketch, "E57", {"start": v(6965.95, -4473.57) * mm, "end": v(8521.7, -4473.57) * mm});
            skLineSegment(sketch, "E58", {"start": v(8521.7, -4473.57) * mm, "end": v(8521.7, -2974.97) * mm});
            skLineSegment(sketch, "E59", {"start": v(8521.7, -2974.97) * mm, "end": v(9156.7, -2974.97) * mm});
            skLineSegment(sketch, "E60", {"start": v(6007.1, -120.65) * mm, "end": v(6007.1, -755.65) * mm});
            skLineSegment(sketch, "E61", {"start": v(6007.1, -755.65) * mm, "end": v(8521.7, -755.65) * mm});
            skLineSegment(sketch, "E62", {"start": v(8521.7, -755.65) * mm, "end": v(8521.7, -1847.85) * mm});
            skLineSegment(sketch, "E63", {"start": v(8521.7, -1847.85) * mm, "end": v(9156.7, -1847.85) * mm});
            skLineSegment(sketch, "E64", {"start": v(6007.1, -120.65) * mm, "end": v(9156.7, -120.65) * mm});
            skLineSegment(sketch, "E65", {"start": v(9156.7, -120.65) * mm, "end": v(9156.7, -1847.85) * mm});
            skLineSegment(sketch, "E66", {"start": v(6965.95, -5108.57) * mm, "end": v(9156.7, -5108.57) * mm});
            skLineSegment(sketch, "E67", {"start": v(9156.7, -5108.57) * mm, "end": v(9156.7, -2974.97) * mm});
            skLineSegment(sketch, "E68.bottom", {"start": v(6108.7, -1771.65) * mm, "end": v(7327.9, -1771.65) * mm});
            skLineSegment(sketch, "E68.top", {"start": v(6108.7, -3457.57) * mm, "end": v(7327.9, -3457.57) * mm});
            skLineSegment(sketch, "E68.left", {"start": v(6108.7, -1771.65) * mm, "end": v(6108.7, -3457.57) * mm});
            skLineSegment(sketch, "E68.right", {"start": v(7327.9, -1771.65) * mm, "end": v(7327.9, -3457.57) * mm});
            skLineSegment(sketch, "E69", {"start": v(3346.45, -4279.9) * mm, "end": v(5314.95, -4279.9) * mm, "construction": true});
            skLineSegment(sketch, "E70", {"start": v(4330.7, -4279.9) * mm, "end": v(4330.7, 382.3) * mm, "construction": true});
            skLineSegment(sketch, "E71", {"start": v(4330.7, -1187.45) * mm, "end": v(3873.5, -1187.45) * mm});
            skLineSegment(sketch, "E72", {"start": v(3873.5, -1187.45) * mm, "end": v(3873.5, -3016.25) * mm});
            skLineSegment(sketch, "E73", {"start": v(3873.5, -3016.25) * mm, "end": v(4330.7, -3016.25) * mm});
            skLineSegment(sketch, "E74.MirrorCS", {"start": v(4330.7, -1187.45) * mm, "end": v(4787.9, -1187.45) * mm});
            skLineSegment(sketch, "E75.MirrorCS", {"start": v(4787.9, -3016.25) * mm, "end": v(4330.7, -3016.25) * mm});
            skLineSegment(sketch, "E76.MirrorCS", {"start": v(4787.9, -1187.45) * mm, "end": v(4787.9, -3016.25) * mm});
            skLineSegment(sketch, "E77", {"start": v(6616.7, -1771.65) * mm, "end": v(6616.7, -3457.57) * mm});
            skLineSegment(sketch, "E78.bottom", {"start": v(4787.9, -1187.45) * mm, "end": v(4533.9, -1187.45) * mm, "construction": true});
            skLineSegment(sketch, "E78.top", {"start": v(4787.9, -1441.45) * mm, "end": v(4533.9, -1441.45) * mm, "construction": true});
            skLineSegment(sketch, "E78.left", {"start": v(4787.9, -1187.45) * mm, "end": v(4787.9, -1441.45) * mm, "construction": true});
            skLineSegment(sketch, "E78.right", {"start": v(4533.9, -1187.45) * mm, "end": v(4533.9, -1441.45) * mm, "construction": true});
            skLineSegment(sketch, "E79.bottom", {"start": v(3873.5, -1187.45) * mm, "end": v(4127.5, -1187.45) * mm, "construction": true});
            skLineSegment(sketch, "E79.top", {"start": v(3873.5, -1441.45) * mm, "end": v(4127.5, -1441.45) * mm, "construction": true});
            skLineSegment(sketch, "E79.left", {"start": v(3873.5, -1187.45) * mm, "end": v(3873.5, -1441.45) * mm, "construction": true});
            skLineSegment(sketch, "E79.right", {"start": v(4127.5, -1187.45) * mm, "end": v(4127.5, -1441.45) * mm, "construction": true});
            skLineSegment(sketch, "E80.bottom", {"start": v(3873.5, -3016.25) * mm, "end": v(4127.5, -3016.25) * mm, "construction": true});
            skLineSegment(sketch, "E80.top", {"start": v(3873.5, -2762.25) * mm, "end": v(4127.5, -2762.25) * mm, "construction": true});
            skLineSegment(sketch, "E80.left", {"start": v(3873.5, -3016.25) * mm, "end": v(3873.5, -2762.25) * mm, "construction": true});
            skLineSegment(sketch, "E80.right", {"start": v(4127.5, -3016.25) * mm, "end": v(4127.5, -2762.25) * mm, "construction": true});
            skLineSegment(sketch, "E81.bottom", {"start": v(4787.9, -3016.25) * mm, "end": v(4533.9, -3016.25) * mm, "construction": true});
            skLineSegment(sketch, "E81.top", {"start": v(4787.9, -2762.25) * mm, "end": v(4533.9, -2762.25) * mm, "construction": true});
            skLineSegment(sketch, "E81.left", {"start": v(4787.9, -3016.25) * mm, "end": v(4787.9, -2762.25) * mm, "construction": true});
            skLineSegment(sketch, "E81.right", {"start": v(4533.9, -3016.25) * mm, "end": v(4533.9, -2762.25) * mm, "construction": true});
            skLineSegment(sketch, "E82.bottom", {"start": v(4533.9, -1441.45) * mm, "end": v(4635.5, -1441.45) * mm});
            skLineSegment(sketch, "E82.top", {"start": v(4533.9, -1339.85) * mm, "end": v(4635.5, -1339.85) * mm});
            skLineSegment(sketch, "E82.left", {"start": v(4533.9, -1441.45) * mm, "end": v(4533.9, -1339.85) * mm});
            skLineSegment(sketch, "E82.right", {"start": v(4635.5, -1441.45) * mm, "end": v(4635.5, -1339.85) * mm});
            skLineSegment(sketch, "E83.bottom", {"start": v(4127.5, -1441.45) * mm, "end": v(4025.9, -1441.45) * mm});
            skLineSegment(sketch, "E83.top", {"start": v(4127.5, -1339.85) * mm, "end": v(4025.9, -1339.85) * mm});
            skLineSegment(sketch, "E83.left", {"start": v(4127.5, -1441.45) * mm, "end": v(4127.5, -1339.85) * mm});
            skLineSegment(sketch, "E83.right", {"start": v(4025.9, -1441.45) * mm, "end": v(4025.9, -1339.85) * mm});
            skLineSegment(sketch, "E84.bottom", {"start": v(4127.5, -2762.25) * mm, "end": v(4025.9, -2762.25) * mm});
            skLineSegment(sketch, "E84.top", {"start": v(4127.5, -2863.85) * mm, "end": v(4025.9, -2863.85) * mm});
            skLineSegment(sketch, "E84.left", {"start": v(4127.5, -2762.25) * mm, "end": v(4127.5, -2863.85) * mm});
            skLineSegment(sketch, "E84.right", {"start": v(4025.9, -2762.25) * mm, "end": v(4025.9, -2863.85) * mm});
            skLineSegment(sketch, "E85.bottom", {"start": v(4533.9, -2762.25) * mm, "end": v(4635.5, -2762.25) * mm});
            skLineSegment(sketch, "E85.top", {"start": v(4533.9, -2863.85) * mm, "end": v(4635.5, -2863.85) * mm});
            skLineSegment(sketch, "E85.left", {"start": v(4533.9, -2762.25) * mm, "end": v(4533.9, -2863.85) * mm});
            skLineSegment(sketch, "E85.right", {"start": v(4635.5, -2762.25) * mm, "end": v(4635.5, -2863.85) * mm});
            skLineSegment(sketch, "E86.bottom", {"start": v(9156.7, -2974.97) * mm, "end": v(8486.99, -2974.97) * mm});
            skLineSegment(sketch, "E86.top", {"start": v(9156.7, -3889.37) * mm, "end": v(8486.99, -3889.37) * mm});
            skLineSegment(sketch, "E86.left", {"start": v(9156.7, -2974.97) * mm, "end": v(9156.7, -3889.37) * mm});
            skLineSegment(sketch, "E86.right", {"start": v(8486.99, -2974.97) * mm, "end": v(8486.99, -3889.37) * mm});
            skArc(sketch, "E87", {"start": v(8486.99, -2974.97) * mm, "mid": v(8445.5, -3432.17) * mm, "end": v(8486.99, -3889.37) * mm});
            skSolve(sketch);
        }
        {
            var Q0;
            {var subQ0=sQuery(id+"F17.wireOp",EDGE,"E68.right");Q0=makeQuery(id+"F17.imprint","IMPRINT",FACE,{"disambiguationData":[TD([[makeQuery(id+"F17.imprint","IMPRINT",EDGE,{"derivedFrom":subQ0}),-1.0]])]});}
            var Q1;
            Q1=makeQuery(id+"F17.imprint","IMPRINT",FACE,{"disambiguationData":[TD([[makeQuery(id+"F17.imprint","IMPRINT",EDGE,{"derivedFrom":sQuery(id+"F17.wireOp",EDGE,"E60")}),1.0]])]});
            var Q2;
            {var subQ0=sQuery(id+"F17.wireOp",EDGE,"E57");Q2=makeQuery(id+"F17.imprint","IMPRINT",FACE,{"disambiguationData":[TD([[makeQuery(id+"F17.imprint","IMPRINT",EDGE,{"derivedFrom":subQ0}),-1.0]])]});}
            extrude(context, id + "F18", {"entities" : qUnion([Q0, Q1, Q2]), "depth" : 914.4 * mm});
        }
        {
            var Q0;
            {var subQ3=sQuery(id+"F17.wireOp",EDGE,"E56.bottom");Q0=makeQuery(id+"F17.imprint","IMPRINT",FACE,{"disambiguationData":[TD([[makeQuery(id+"F17.imprint","IMPRINT",EDGE,{"derivedFrom":subQ3}),1.0]])]});}
            extrude(context, id + "F19", {"entities" : qUnion([Q0]), "operationType" : NewBodyOperationType.ADD, "depth" : 2438.4 * mm});
        }
        {
            var Q0;
            Q0=makeQuery(id+"F17.imprint","IMPRINT",FACE,{"disambiguationData":[TD([[makeQuery(id+"F17.imprint","IMPRINT",EDGE,{"derivedFrom":sQuery(id+"F17.wireOp",EDGE,"E71")}),1.0]])]});
            extrude(context, id + "F20", {"entities" : qUnion([Q0]), "depth" : 762 * mm, "hasSecondDirection" : true, "secondDirectionOppositeDirection" : false, "secondDirectionDepth" : 711.2 * mm});
        }
        {
            var Q0;
            Q0=makeQuery(id+"F18.opExtrude","CAP_FACE",FACE,{"disambiguationData":[OSD([sQuery(id+"F17.wireOp",EDGE,"E60"),sQuery(id+"F17.wireOp",EDGE,"E61"),sQuery(id+"F17.wireOp",EDGE,"E62"),sQuery(id+"F17.wireOp",EDGE,"E63"),sQuery(id+"F17.wireOp",EDGE,"E64"),sQuery(id+"F17.wireOp",EDGE,"E65")])],"isStart":false});
            cPlane(context, id + "F21", {"entities" : qUnion([Q0]), "cplaneType" : CPlaneType.OFFSET, "offset" : 50.8 * mm, "width" : 152.4 * mm, "height" : 152.4 * mm});
        }
        {
            var Q0;
            Q0=qCreatedBy(id+"F21.planeOp",FACE);
            var sketch = newSketch(context, id + "F22", { "sketchPlane" : qUnion([Q0])});
            skLineSegment(sketch, "E88.bottom", {"start": v(7124.7, -298.45) * mm, "end": v(7886.7, -298.45) * mm});
            skLineSegment(sketch, "E88.top", {"start": v(7124.7, -806.45) * mm, "end": v(7886.7, -806.45) * mm});
            skLineSegment(sketch, "E88.left", {"start": v(7124.7, -298.45) * mm, "end": v(7124.7, -806.45) * mm});
            skLineSegment(sketch, "E88.right", {"start": v(7886.7, -298.45) * mm, "end": v(7886.7, -806.45) * mm});
            skLineSegment(sketch, "E89", {"start": v(7505.7, -298.45) * mm, "end": v(7505.7, -806.45) * mm, "construction": true});
            skSolve(sketch);
        }
        {
            var Q0;
            {var subQ0=sQuery(id+"F22.wireOp",EDGE,"E88.bottom");Q0=makeQuery(id+"F22.imprint","IMPRINT",FACE,{"disambiguationData":[TD([[makeQuery(id+"F22.imprint","IMPRINT",EDGE,{"derivedFrom":subQ0}),-1.0]])]});}
            var Q1;
            {var subQ0=sQuery(id+"F22.wireOp",EDGE,"E88.top");Q1=makeQuery(id+"F22.imprint","IMPRINT",FACE,{"disambiguationData":[TD([[makeQuery(id+"F22.imprint","IMPRINT",EDGE,{"derivedFrom":subQ0}),1.0]])]});}
            extrude(context, id + "F23", {"entities" : qUnion([Q0, Q1]), "oppositeDirection" : true, "depth" : 304.8 * mm});
        }
        {
            var Q0;
            Q0=qCreatedBy(id+"F21.planeOp",FACE);
            var sketch = newSketch(context, id + "F24", { "sketchPlane" : qUnion([Q0])});
            skLineSegment(sketch, "E90.bottom", {"start": v(6819.9, -2233.61) * mm, "end": v(7378.7, -2233.61) * mm});
            skLineSegment(sketch, "E90.top", {"start": v(6819.9, -2995.61) * mm, "end": v(7378.7, -2995.61) * mm});
            skLineSegment(sketch, "E90.left", {"start": v(6819.9, -2233.61) * mm, "end": v(6819.9, -2995.61) * mm});
            skLineSegment(sketch, "E90.right", {"start": v(7378.7, -2233.61) * mm, "end": v(7378.7, -2995.61) * mm});
            skLineSegment(sketch, "E91.0", {"start": v(7327.9, -1771.65) * mm, "end": v(7327.9, -3457.57) * mm});
            skLineSegment(sketch, "E92", {"start": v(7327.9, -2614.61) * mm, "end": v(6453.7, -2614.61) * mm, "construction": true});
            skSolve(sketch);
        }
        {
            var Q0;
            Q0=makeQuery(id+"F24.imprint","IMPRINT",FACE,{"disambiguationData":[TD([[makeQuery(id+"F24.imprint","IMPRINT",EDGE,{"derivedFrom":sQuery(id+"F24.wireOp",EDGE,"E90.bottom")}),-1.0]])]});
            var Q1;
            Q1=makeQuery(id+"F18.opExtrude","CAP_FACE",FACE,{"disambiguationData":[OSD([sQuery(id+"F17.wireOp",EDGE,"E68.bottom"),sQuery(id+"F17.wireOp",EDGE,"E68.top"),sQuery(id+"F17.wireOp",EDGE,"E68.left"),sQuery(id+"F17.wireOp",EDGE,"E68.right")])],"isStart":true});
            extrude(context, id + "F25", {"entities" : qUnion([Q0]), "endBound" : BoundingType.UP_TO_SURFACE, "oppositeDirection" : true, "endBoundEntityFace" : qUnion([Q1]), "depth" : 25.4 * mm});
        }
        {
            var Q0;
            {var subQ0=sQuery(id+"F17.wireOp",EDGE,"E68.left");Q0=makeQuery(id+"F17.imprint","IMPRINT",FACE,{"disambiguationData":[TD([[makeQuery(id+"F17.imprint","IMPRINT",EDGE,{"derivedFrom":subQ0}),1.0]])]});}
            var Q1;
            Q1=makeQuery(id+"F18.opExtrude","CAP_FACE",FACE,{"disambiguationData":[OSD([sQuery(id+"F17.wireOp",EDGE,"E68.bottom"),sQuery(id+"F17.wireOp",EDGE,"E68.top"),sQuery(id+"F17.wireOp",EDGE,"E68.right"),sQuery(id+"F17.wireOp",EDGE,"E77")])],"isStart":false});
            extrude(context, id + "F26", {"entities" : qUnion([Q0]), "operationType" : NewBodyOperationType.ADD, "endBound" : BoundingType.UP_TO_SURFACE, "endBoundEntityFace" : qUnion([Q1]), "depth" : 1066.8 * mm});
        }
        {
            var Q0;
            Q0=makeQuery(id+"F16.boolean.opBoolean","MERGE",FACE,{"derivedFrom":[makeQuery(id+"F1.opExtrude","CAP_FACE",FACE,{"disambiguationData":[OSD([sQuery(id+"F0.wireOp",EDGE,"E0.bottom"),sQuery(id+"F0.wireOp",EDGE,"E0.left"),sQuery(id+"F0.wireOp",EDGE,"E0.right"),sQuery(id+"F0.wireOp",EDGE,"E1.bottom"),sQuery(id+"F0.wireOp",EDGE,"E1.top"),sQuery(id+"F0.wireOp",EDGE,"E1.right"),sQuery(id+"F0.wireOp",EDGE,"E2.left"),sQuery(id+"F0.wireOp",EDGE,"E2.right"),sQuery(id+"F0.wireOp",EDGE,"E3.top"),sQuery(id+"F0.wireOp",EDGE,"E3.left"),sQuery(id+"F0.wireOp",EDGE,"E3.right"),sQuery(id+"F0.wireOp",EDGE,"E4.bottom"),sQuery(id+"F0.wireOp",EDGE,"E4.top"),sQuery(id+"F0.wireOp",EDGE,"E5.bottom"),sQuery(id+"F0.wireOp",EDGE,"E5.top"),sQuery(id+"F0.wireOp",EDGE,"E5.right"),sQuery(id+"F0.wireOp",EDGE,"E6.left"),sQuery(id+"F0.wireOp",EDGE,"E6.right"),sQuery(id+"F0.wireOp",EDGE,"E7.bottom"),sQuery(id+"F0.wireOp",EDGE,"E7.top"),sQuery(id+"F0.wireOp",EDGE,"E7.left"),sQuery(id+"F0.wireOp",EDGE,"E8.bottom"),sQuery(id+"F0.wireOp",EDGE,"E8.top"),sQuery(id+"F0.wireOp",EDGE,"E9.bottom"),sQuery(id+"F0.wireOp",EDGE,"E9.top"),sQuery(id+"F0.wireOp",EDGE,"E9.right"),sQuery(id+"F0.wireOp",EDGE,"E10.top"),sQuery(id+"F0.wireOp",EDGE,"E10.left"),sQuery(id+"F0.wireOp",EDGE,"E10.right"),sQuery(id+"F0.wireOp",EDGE,"E11.bottom"),sQuery(id+"F0.wireOp",EDGE,"E11.top"),sQuery(id+"F0.wireOp",EDGE,"E12.bottom"),sQuery(id+"F0.wireOp",EDGE,"E12.top"),sQuery(id+"F0.wireOp",EDGE,"E13.left"),sQuery(id+"F0.wireOp",EDGE,"E13.right"),sQuery(id+"F0.wireOp",EDGE,"E14.bottom"),sQuery(id+"F0.wireOp",EDGE,"E14.top"),sQuery(id+"F0.wireOp",EDGE,"E15.bottom"),sQuery(id+"F0.wireOp",EDGE,"E15.top"),sQuery(id+"F0.wireOp",EDGE,"E16.bottom"),sQuery(id+"F0.wireOp",EDGE,"E16.top"),sQuery(id+"F0.wireOp",EDGE,"E16.right"),sQuery(id+"F0.wireOp",EDGE,"E17.left"),sQuery(id+"F0.wireOp",EDGE,"E17.right"),sQuery(id+"F0.wireOp",EDGE,"E18.left"),sQuery(id+"F0.wireOp",EDGE,"E18.right"),sQuery(id+"F0.wireOp",EDGE,"E19.bottom"),sQuery(id+"F0.wireOp",EDGE,"E19.top"),sQuery(id+"F0.wireOp",EDGE,"E19.right"),sQuery(id+"F0.wireOp",EDGE,"E20.left"),sQuery(id+"F0.wireOp",EDGE,"E20.right"),sQuery(id+"F0.wireOp",EDGE,"E21.bottom"),sQuery(id+"F0.wireOp",EDGE,"E21.top"),sQuery(id+"F0.wireOp",EDGE,"E21.right"),sQuery(id+"F0.wireOp",EDGE,"E22.left"),sQuery(id+"F0.wireOp",EDGE,"E22.right"),sQuery(id+"F0.wireOp",EDGE,"E23"),sQuery(id+"F0.wireOp",EDGE,"E24"),sQuery(id+"F0.wireOp",EDGE,"E25"),sQuery(id+"F0.wireOp",EDGE,"E26"),sQuery(id+"F0.wireOp",EDGE,"E27"),sQuery(id+"F0.wireOp",EDGE,"E28"),sQuery(id+"F0.wireOp",EDGE,"E29"),sQuery(id+"F0.wireOp",EDGE,"E30"),sQuery(id+"F0.wireOp",EDGE,"E31"),sQuery(id+"F0.wireOp",EDGE,"E32"),sQuery(id+"F0.wireOp",EDGE,"E33.0"),sQuery(id+"F0.wireOp",EDGE,"E33.1"),sQuery(id+"F0.wireOp",EDGE,"E33.2"),sQuery(id+"F0.wireOp",EDGE,"E33.3"),sQuery(id+"F0.wireOp",EDGE,"E33.4"),sQuery(id+"F0.wireOp",EDGE,"E33.5"),sQuery(id+"F0.wireOp",EDGE,"E33.6"),sQuery(id+"F0.wireOp",EDGE,"E33.7"),sQuery(id+"F0.wireOp",EDGE,"E33.8"),sQuery(id+"F0.wireOp",EDGE,"E34"),sQuery(id+"F0.wireOp",EDGE,"E35")])],"isStart":false}),makeQuery(id+"F16.opExtrude","CAP_FACE",FACE,{"disambiguationData":[OSD([sQuery(id+"F15.wireOp",EDGE,"E54.bottom"),sQuery(id+"F15.wireOp",EDGE,"E54.top"),sQuery(id+"F15.wireOp",EDGE,"E54.left"),sQuery(id+"F15.wireOp",EDGE,"E54.right")])],"isStart":true})]});
            var sketch = newSketch(context, id + "F27", { "sketchPlane" : qUnion([Q0])});
            skLineSegment(sketch, "E93.0", {"start": v(9156.7, -120.65) * mm, "end": v(8851.9, -120.65) * mm});
            skLineSegment(sketch, "E94.0", {"start": v(9156.7, -5108.57) * mm, "end": v(9156.7, -3889.37) * mm});
            skLineSegment(sketch, "E95", {"start": v(8851.9, -120.65) * mm, "end": v(8851.9, -1847.85) * mm});
            skLineSegment(sketch, "E96", {"start": v(8851.9, -1847.85) * mm, "end": v(9156.7, -1847.85) * mm});
            skLineSegment(sketch, "E97", {"start": v(9156.7, -3889.37) * mm, "end": v(8851.9, -3889.37) * mm});
            skLineSegment(sketch, "E98", {"start": v(8851.9, -3889.37) * mm, "end": v(8851.9, -5108.57) * mm});
            skLineSegment(sketch, "E99", {"start": v(8851.9, -5108.57) * mm, "end": v(9156.7, -5108.57) * mm});
            skPoint(sketch, "E100.orphan", {"position": v(120.65, -120.65) * mm});
            skLineSegment(sketch, "E101.trimOffspring", {"start": v(9156.7, -1847.85) * mm, "end": v(9156.7, -120.65) * mm});
            skLineSegment(sketch, "E102.top", {"start": v(9156.7, -2974.97) * mm, "end": v(8851.9, -2974.97) * mm});
            skLineSegment(sketch, "E102.left", {"start": v(9156.7, -3889.37) * mm, "end": v(9156.7, -2974.97) * mm});
            skLineSegment(sketch, "E102.right", {"start": v(8851.9, -3889.37) * mm, "end": v(8851.9, -2974.97) * mm});
            skSolve(sketch);
        }
        {
            var Q0;
            Q0=makeQuery(id+"F27.imprint","IMPRINT",FACE,{"disambiguationData":[TD([[makeQuery(id+"F27.imprint","IMPRINT",EDGE,{"derivedFrom":sQuery(id+"F27.wireOp",EDGE,"E93.0")}),1.0]])]});
            var Q1;
            Q1=makeQuery(id+"F27.imprint","IMPRINT",FACE,{"disambiguationData":[TD([[makeQuery(id+"F27.imprint","IMPRINT",EDGE,{"derivedFrom":sQuery(id+"F27.wireOp",EDGE,"E94.0")}),1.0]])]});
            extrude(context, id + "F28", {"entities" : qUnion([Q0, Q1]), "oppositeDirection" : true, "depth" : 1016 * mm});
        }
        {
            var Q0;
            Q0=makeQuery(id+"F17.imprint","IMPRINT",FACE,{"disambiguationData":[TD([[makeQuery(id+"F17.imprint","IMPRINT",EDGE,{"derivedFrom":sQuery(id+"F17.wireOp",EDGE,"E82.bottom")}),1.0]])]});
            var Q1;
            Q1=makeQuery(id+"F17.imprint","IMPRINT",FACE,{"disambiguationData":[TD([[makeQuery(id+"F17.imprint","IMPRINT",EDGE,{"derivedFrom":sQuery(id+"F17.wireOp",EDGE,"E83.bottom")}),-1.0]])]});
            var Q2;
            Q2=makeQuery(id+"F17.imprint","IMPRINT",FACE,{"disambiguationData":[TD([[makeQuery(id+"F17.imprint","IMPRINT",EDGE,{"derivedFrom":sQuery(id+"F17.wireOp",EDGE,"E84.bottom")}),1.0]])]});
            var Q3;
            Q3=makeQuery(id+"F17.imprint","IMPRINT",FACE,{"disambiguationData":[TD([[makeQuery(id+"F17.imprint","IMPRINT",EDGE,{"derivedFrom":sQuery(id+"F17.wireOp",EDGE,"E85.bottom")}),-1.0]])]});
            var Q4;
            Q4=makeQuery(id+"F20.opExtrude","CAP_FACE",FACE,{"disambiguationData":[OSD([sQuery(id+"F17.wireOp",EDGE,"E71"),sQuery(id+"F17.wireOp",EDGE,"E72"),sQuery(id+"F17.wireOp",EDGE,"E73"),sQuery(id+"F17.wireOp",EDGE,"E74.MirrorCS"),sQuery(id+"F17.wireOp",EDGE,"E75.MirrorCS"),sQuery(id+"F17.wireOp",EDGE,"E76.MirrorCS"),sQuery(id+"F17.wireOp",EDGE,"E82.bottom"),sQuery(id+"F17.wireOp",EDGE,"E82.top"),sQuery(id+"F17.wireOp",EDGE,"E82.left"),sQuery(id+"F17.wireOp",EDGE,"E82.right"),sQuery(id+"F17.wireOp",EDGE,"E83.bottom"),sQuery(id+"F17.wireOp",EDGE,"E83.top"),sQuery(id+"F17.wireOp",EDGE,"E83.left"),sQuery(id+"F17.wireOp",EDGE,"E83.right"),sQuery(id+"F17.wireOp",EDGE,"E84.bottom"),sQuery(id+"F17.wireOp",EDGE,"E84.top"),sQuery(id+"F17.wireOp",EDGE,"E84.left"),sQuery(id+"F17.wireOp",EDGE,"E84.right"),sQuery(id+"F17.wireOp",EDGE,"E85.bottom"),sQuery(id+"F17.wireOp",EDGE,"E85.top"),sQuery(id+"F17.wireOp",EDGE,"E85.left"),sQuery(id+"F17.wireOp",EDGE,"E85.right")])],"isStart":false});
            extrude(context, id + "F29", {"entities" : qUnion([Q0, Q1, Q2, Q3]), "operationType" : NewBodyOperationType.ADD, "endBound" : BoundingType.UP_TO_SURFACE, "endBoundEntityFace" : qUnion([Q4]), "depth" : 25.4 * mm});
        }
        {
            var Q0;
            Q0=qCreatedBy(makeId("Top.planeOp"),FACE);
            var sketch = newSketch(context, id + "F30", { "sketchPlane" : qUnion([Q0])});
            skLineSegment(sketch, "E103.0", {"start": v(120.65, -2200.27) * mm, "end": v(120.65, -2999.89) * mm});
            skLineSegment(sketch, "E104", {"start": v(120.65, -2200.27) * mm, "end": v(1715.64, -2200.27) * mm, "construction": true});
            skLineSegment(sketch, "E105", {"start": v(120.65, -2999.89) * mm, "end": v(606.92, -2999.89) * mm});
            skLineSegment(sketch, "E106", {"start": v(606.92, -2999.89) * mm, "end": v(606.92, -2200.27) * mm});
            skLineSegment(sketch, "E107", {"start": v(218.24, -2999.89) * mm, "end": v(218.24, -2200.27) * mm});
            skPoint(sketch, "E108.orphan", {"position": v(120.65, -120.65) * mm});
            skPoint(sketch, "E109.orphan", {"position": v(120.65, -4279.9) * mm});
            skLineSegment(sketch, "E110.MirrorCS", {"start": v(120.65, -2200.27) * mm, "end": v(120.65, -1400.66) * mm});
            skLineSegment(sketch, "E111.MirrorCS", {"start": v(606.92, -1400.66) * mm, "end": v(606.92, -2200.27) * mm});
            skLineSegment(sketch, "E112.MirrorCS", {"start": v(120.65, -1400.66) * mm, "end": v(606.92, -1400.66) * mm});
            skLineSegment(sketch, "E113.MirrorCS", {"start": v(218.24, -1400.66) * mm, "end": v(218.24, -2200.27) * mm});
            skSolve(sketch);
        }
        {
            var Q0;
            {var subQ2=sQuery(id+"F30.wireOp",EDGE,"E103.0");Q0=makeQuery(id+"F30.imprint","IMPRINT",FACE,{"disambiguationData":[TD([[makeQuery(id+"F30.imprint","IMPRINT",EDGE,{"derivedFrom":subQ2}),1.0]])]});}
            extrude(context, id + "F31", {"entities" : qUnion([Q0]), "depth" : 1117.6 * mm});
        }
        {
            var Q0;
            {var subQ2=sQuery(id+"F30.wireOp",EDGE,"E106");Q0=makeQuery(id+"F30.imprint","IMPRINT",FACE,{"disambiguationData":[TD([[makeQuery(id+"F30.imprint","IMPRINT",EDGE,{"derivedFrom":subQ2}),1.0]])]});}
            extrude(context, id + "F32", {"entities" : qUnion([Q0]), "operationType" : NewBodyOperationType.ADD, "depth" : 50.8 * mm});
        }
        {
            var Q0;
            Q0=makeQuery(id+"F31.opExtrude","CAP_FACE",FACE,{"disambiguationData":[OSD([sQuery(id+"F30.wireOp",EDGE,"E103.0"),sQuery(id+"F30.wireOp",EDGE,"E105"),sQuery(id+"F30.wireOp",EDGE,"E107"),sQuery(id+"F30.wireOp",EDGE,"E110.MirrorCS"),sQuery(id+"F30.wireOp",EDGE,"E112.MirrorCS"),sQuery(id+"F30.wireOp",EDGE,"E113.MirrorCS")])],"isStart":false});
            var sketch = newSketch(context, id + "F33", { "sketchPlane" : qUnion([Q0])});
            skLineSegment(sketch, "E114.0", {"start": v(120.65, -2999.89) * mm, "end": v(120.65, -1400.66) * mm});
            skLineSegment(sketch, "E115.0", {"start": v(120.65, -1400.66) * mm, "end": v(374.65, -1400.66) * mm});
            skLineSegment(sketch, "E116.0", {"start": v(120.65, -2999.89) * mm, "end": v(374.65, -2999.89) * mm});
            skLineSegment(sketch, "E117", {"start": v(374.65, -1400.66) * mm, "end": v(374.65, -2999.89) * mm});
            skPoint(sketch, "E118.orphan", {"position": v(218.24, -1400.66) * mm});
            skPoint(sketch, "E119.orphan", {"position": v(218.24, -2999.89) * mm});
            skLineSegment(sketch, "E120.top", {"start": v(120.65, -4279.9) * mm, "end": v(374.65, -4279.9) * mm});
            skLineSegment(sketch, "E120.left", {"start": v(120.65, -2999.89) * mm, "end": v(120.65, -4279.9) * mm});
            skLineSegment(sketch, "E120.right", {"start": v(374.65, -2999.89) * mm, "end": v(374.65, -4279.9) * mm});
            skLineSegment(sketch, "E121.top", {"start": v(120.65, -120.65) * mm, "end": v(374.65, -120.65) * mm});
            skLineSegment(sketch, "E121.left", {"start": v(120.65, -1400.66) * mm, "end": v(120.65, -120.65) * mm});
            skLineSegment(sketch, "E121.right", {"start": v(374.65, -1400.66) * mm, "end": v(374.65, -120.65) * mm});
            skSolve(sketch);
        }
        {
            var Q0;
            {var subQ2=sQuery(id+"F33.wireOp",EDGE,"E117");Q0=makeQuery(id+"F33.imprint","IMPRINT",FACE,{"disambiguationData":[TD([[makeQuery(id+"F33.imprint","IMPRINT",EDGE,{"derivedFrom":subQ2}),-1.0]])]});}
            var Q1;
            {var subQ0=sQuery(id+"F33.wireOp",EDGE,"E114.0");Q1=makeQuery(id+"F33.imprint","IMPRINT",FACE,{"disambiguationData":[TD([[makeQuery(id+"F33.imprint","IMPRINT",EDGE,{"derivedFrom":subQ0}),-1.0]])]});}
            extrude(context, id + "F34", {"entities" : qUnion([Q0, Q1]), "depth" : 101.6 * mm});
        }
        {
            var Q0;
            Q0=makeQuery(id+"F31.opExtrude","SWEPT_FACE",FACE,{"disambiguationData":[OSD([sQuery(id+"F30.wireOp",EDGE,"E107"),sQuery(id+"F30.wireOp",EDGE,"E113.MirrorCS")])]});
            var sketch = newSketch(context, id + "F35", { "sketchPlane" : qUnion([Q0])});
            skLineSegment(sketch, "E122.0", {"start": v(-2708.27, 50.8) * mm, "end": v(-2200.27, 50.8) * mm});
            skLineSegment(sketch, "E123", {"start": v(-2200.27, 50.8) * mm, "end": v(-2200.27, 814.65) * mm, "construction": true});
            skLineSegment(sketch, "E124", {"start": v(-2708.27, 50.8) * mm, "end": v(-2708.27, 812.8) * mm});
            skLineSegment(sketch, "E125", {"start": v(-2708.27, 812.8) * mm, "end": v(-2200.27, 812.8) * mm});
            skPoint(sketch, "E126.orphan", {"position": v(-2999.89, 50.8) * mm});
            skPoint(sketch, "E127.orphan", {"position": v(-1400.66, 50.8) * mm});
            skLineSegment(sketch, "E128.MirrorCS", {"start": v(-1692.27, 50.8) * mm, "end": v(-1692.27, 812.8) * mm});
            skLineSegment(sketch, "E129.MirrorCS", {"start": v(-1692.27, 812.8) * mm, "end": v(-2200.27, 812.8) * mm});
            skLineSegment(sketch, "E130.MirrorCS", {"start": v(-1692.27, 50.8) * mm, "end": v(-2200.27, 50.8) * mm});
            skSolve(sketch);
        }
        {
            var Q0;
            Q0=makeQuery(id+"F35.imprint","IMPRINT",FACE,{"disambiguationData":[TD([[makeQuery(id+"F35.imprint","IMPRINT",EDGE,{"derivedFrom":sQuery(id+"F35.wireOp",EDGE,"E122.0")}),1.0]])]});
            extrude(context, id + "F36", {"entities" : qUnion([Q0]), "depth" : 152.4 * mm});
        }
        {
            var Q0;
            Q0=makeQuery(id+"F36.opExtrude","CAP_EDGE",EDGE,{"disambiguationData":[OSD([sQuery(id+"F35.wireOp",EDGE,"E125"),sQuery(id+"F35.wireOp",EDGE,"E129.MirrorCS")])],"isStart":false});
            chamfer(context, id + "F37", {"entities" : qUnion([Q0]), "width" : 127 * mm, "tangentPropagation" : true});
        }
        {
            var Q0;
            {var subQ0=sQuery(id+"F0.wireOp",EDGE,"E33.6");Q0=makeQuery(id+"F1.opExtrude","SWEPT_FACE",FACE,{"disambiguationData":[OSD([subQ0]),TDD([makeQuery(id+"F0.imprint","IMPRINT",EDGE,{"disambiguationData":[TD([[makeQuery(id+"F0.imprint","INTERSECT",VERTEX,{"derivedFrom":[sQuery(id+"F0.wireOp",EDGE,"E5.bottom"),subQ0]}),1.0]])],"derivedFrom":subQ0})])]});}
            var sketch = newSketch(context, id + "F38", { "sketchPlane" : qUnion([Q0])});
            skLineSegment(sketch, "E131.0", {"start": v(-120.65, 0) * mm, "end": v(-4279.9, 0) * mm});
            skLineSegment(sketch, "E132.0", {"start": v(-4279.9, 2425.7) * mm, "end": v(-4279.9, 0) * mm});
            skLineSegment(sketch, "E133.0", {"start": v(-2999.89, 1117.6) * mm, "end": v(-2999.89, 0) * mm});
            skLineSegment(sketch, "E134.0", {"start": v(-120.65, 2425.7) * mm, "end": v(-120.65, 0) * mm});
            skLineSegment(sketch, "E135.0", {"start": v(-1400.66, 1117.6) * mm, "end": v(-1400.66, 0) * mm});
            skLineSegment(sketch, "E136", {"start": v(-2999.89, 914.4) * mm, "end": v(-4279.9, 914.4) * mm});
            skLineSegment(sketch, "E137", {"start": v(-1400.66, 914.4) * mm, "end": v(-120.65, 914.4) * mm});
            skSolve(sketch);
        }
        {
            var Q0;
            {var subQ3=sQuery(id+"F38.wireOp",EDGE,"E133.0");Q0=makeQuery(id+"F38.imprint","IMPRINT",FACE,{"disambiguationData":[TD([[makeQuery(id+"F38.imprint","IMPRINT",EDGE,{"derivedFrom":subQ3}),-1.0]])]});}
            var Q1;
            {var subQ3=sQuery(id+"F38.wireOp",EDGE,"E135.0");Q1=makeQuery(id+"F38.imprint","IMPRINT",FACE,{"disambiguationData":[TD([[makeQuery(id+"F38.imprint","IMPRINT",EDGE,{"derivedFrom":subQ3}),1.0]])]});}
            extrude(context, id + "F39", {"entities" : qUnion([Q0, Q1]), "depth" : 381 * mm});
        }
        {
            var Q0;
            Q0=makeQuery(id+"F39.opExtrude","SWEPT_FACE",FACE,{"disambiguationData":[OSD([sQuery(id+"F38.wireOp",EDGE,"E136")])]});
            var sketch = newSketch(context, id + "F40", { "sketchPlane" : qUnion([Q0])});
            skLineSegment(sketch, "E138.0", {"start": v(120.65, -2999.89) * mm, "end": v(120.65, -4279.9) * mm});
            skLineSegment(sketch, "E139.0", {"start": v(120.65, -1400.66) * mm, "end": v(120.65, -120.65) * mm});
            skLineSegment(sketch, "E140.bottom", {"start": v(120.65, -4279.9) * mm, "end": v(527.05, -4279.9) * mm});
            skLineSegment(sketch, "E140.top", {"start": v(120.65, -2999.89) * mm, "end": v(527.05, -2999.89) * mm});
            skLineSegment(sketch, "E140.left", {"start": v(120.65, -4279.9) * mm, "end": v(120.65, -2999.89) * mm});
            skLineSegment(sketch, "E140.right", {"start": v(527.05, -4279.9) * mm, "end": v(527.05, -2999.89) * mm});
            skLineSegment(sketch, "E141.bottom", {"start": v(120.65, -1400.66) * mm, "end": v(527.05, -1400.66) * mm});
            skLineSegment(sketch, "E141.top", {"start": v(120.65, -120.65) * mm, "end": v(527.05, -120.65) * mm});
            skLineSegment(sketch, "E141.right", {"start": v(527.05, -1400.66) * mm, "end": v(527.05, -120.65) * mm});
            skSolve(sketch);
        }
        {
            var Q0;
            Q0 = qSketchRegion(id + "F40", true);
            extrude(context, id + "F41", {"entities" : qUnion([Q0]), "depth" : 50.8 * mm});
        }
        {
            var Q0;
            Q0=makeQuery(id+"F27.imprint","IMPRINT",FACE,{"disambiguationData":[TD([[makeQuery(id+"F27.imprint","IMPRINT",EDGE,{"derivedFrom":sQuery(id+"F27.wireOp",EDGE,"E97")}),-1.0]])]});
            extrude(context, id + "F42", {"entities" : qUnion([Q0]), "operationType" : NewBodyOperationType.ADD, "oppositeDirection" : true, "depth" : 609.6 * mm});
        }
        {
            var Q0;
            {var subQ5=sQuery(id+"F17.wireOp",EDGE,"E86.left");Q0=makeQuery(id+"F17.imprint","IMPRINT",FACE,{"disambiguationData":[TD([[makeQuery(id+"F17.imprint","IMPRINT",EDGE,{"derivedFrom":subQ5}),-1.0]])]});}
            var Q1;
            {var subQ6=sQuery(id+"F17.wireOp",EDGE,"E86.right");Q1=makeQuery(id+"F17.imprint","IMPRINT",FACE,{"disambiguationData":[TD([[makeQuery(id+"F17.imprint","IMPRINT",EDGE,{"derivedFrom":subQ6}),1.0]])]});}
            var Q2;
            Q2=makeQuery(id+"F17.imprint","IMPRINT",FACE,{"disambiguationData":[TD([[makeQuery(id+"F17.imprint","IMPRINT",EDGE,{"derivedFrom":sQuery(id+"F17.wireOp",EDGE,"E86.right")}),-1.0]])]});
            extrude(context, id + "F43", {"entities" : qUnion([Q0, Q1, Q2]), "depth" : 1778 * mm});
        }
        {
            var Q0;
            Q0=qCreatedBy(makeId("Top.planeOp"),FACE);
            var sketch = newSketch(context, id + "F44", { "sketchPlane" : qUnion([Q0])});
            skLineSegment(sketch, "E142.bottom", {"start": v(5924.55, -4467.22) * mm, "end": v(5010.15, -4467.22) * mm});
            skLineSegment(sketch, "E142.top", {"start": v(5924.55, -4581.52) * mm, "end": v(5010.15, -4581.52) * mm});
            skLineSegment(sketch, "E142.left", {"start": v(5924.55, -4467.22) * mm, "end": v(5924.55, -4581.52) * mm});
            skLineSegment(sketch, "E142.right", {"start": v(5010.15, -4467.22) * mm, "end": v(5010.15, -4581.52) * mm});
            skSolve(sketch);
        }
        {
            var Q0;
            Q0=makeQuery(id+"F44.imprint","IMPRINT",FACE,{"disambiguationData":[TD([[makeQuery(id+"F44.imprint","IMPRINT",EDGE,{"derivedFrom":sQuery(id+"F44.wireOp",EDGE,"E142.bottom")}),1.0]])]});
            extrude(context, id + "F45", {"entities" : qUnion([Q0]), "operationType" : NewBodyOperationType.ADD, "depth" : 1016 * mm});
        }
        {
            var Q0;
            Q0=qCreatedBy(makeId("Top.planeOp"),FACE);
            var sketch = newSketch(context, id + "F46", { "sketchPlane" : qUnion([Q0])});
            skLineSegment(sketch, "E143.0", {"start": v(5924.55, -4581.52) * mm, "end": v(5924.55, -5229.22) * mm});
            skLineSegment(sketch, "E144.0", {"start": v(5924.55, -4581.52) * mm, "end": v(5010.15, -4581.52) * mm});
            skLineSegment(sketch, "E145.bottom", {"start": v(5010.15, -4581.52) * mm, "end": v(5924.55, -4581.52) * mm});
            skLineSegment(sketch, "E145.top", {"start": v(5010.15, -4886.32) * mm, "end": v(5924.55, -4886.32) * mm});
            skLineSegment(sketch, "E145.left", {"start": v(5010.15, -4581.52) * mm, "end": v(5010.15, -4886.32) * mm});
            skLineSegment(sketch, "E145.right", {"start": v(5924.55, -4581.52) * mm, "end": v(5924.55, -4886.32) * mm});
            skLineSegment(sketch, "E146.bottom", {"start": v(5924.55, -5229.22) * mm, "end": v(5619.75, -5229.22) * mm});
            skLineSegment(sketch, "E146.top", {"start": v(5924.55, -4886.32) * mm, "end": v(5619.75, -4886.32) * mm});
            skLineSegment(sketch, "E146.left", {"start": v(5924.55, -5229.22) * mm, "end": v(5924.55, -4886.32) * mm});
            skLineSegment(sketch, "E146.right", {"start": v(5619.75, -5229.22) * mm, "end": v(5619.75, -4886.32) * mm});
            skSolve(sketch);
        }
        {
            var Q0;
            Q0=makeQuery(id+"F46.imprint","IMPRINT",FACE,{"disambiguationData":[TD([[makeQuery(id+"F46.imprint","IMPRINT",EDGE,{"derivedFrom":sQuery(id+"F46.wireOp",EDGE,"E145.bottom")}),-1.0]])]});
            var Q1;
            Q1=makeQuery(id+"F46.imprint","IMPRINT",FACE,{"disambiguationData":[TD([[makeQuery(id+"F46.imprint","IMPRINT",EDGE,{"derivedFrom":sQuery(id+"F46.wireOp",EDGE,"E146.bottom")}),-1.0]])]});
            extrude(context, id + "F47", {"entities" : qUnion([Q0, Q1]), "depth" : 457.2 * mm});
        }
        {
            var Q0;
            Q0=makeQuery(id+"F45.opExtrude","CAP_FACE",FACE,{"disambiguationData":[OSD([sQuery(id+"F44.wireOp",EDGE,"E142.bottom"),sQuery(id+"F44.wireOp",EDGE,"E142.top"),sQuery(id+"F44.wireOp",EDGE,"E142.left"),sQuery(id+"F44.wireOp",EDGE,"E142.right")])],"isStart":false});
            extrude(context, id + "F48", {"entities" : qUnion([Q0]), "depth" : 50.8 * mm});
        }
        {
            var Q0;
            Q0=makeQuery(id+"F18.opExtrude","CAP_FACE",FACE,{"disambiguationData":[OSD([sQuery(id+"F17.wireOp",EDGE,"E60"),sQuery(id+"F17.wireOp",EDGE,"E61"),sQuery(id+"F17.wireOp",EDGE,"E62"),sQuery(id+"F17.wireOp",EDGE,"E63"),sQuery(id+"F17.wireOp",EDGE,"E64"),sQuery(id+"F17.wireOp",EDGE,"E65")])],"isStart":false});
            var Q1;
            {var subQ0=sQuery(id+"F17.wireOp",EDGE,"E77");var subQ1=sQuery(id+"F17.wireOp",EDGE,"E68.right");var subQ2=sQuery(id+"F17.wireOp",EDGE,"E68.top");var subQ3=sQuery(id+"F17.wireOp",EDGE,"E68.bottom");Q1=makeQuery(id+"F26.boolean.opBoolean","MERGE",FACE,{"derivedFrom":[makeQuery(id+"F18.opExtrude","CAP_FACE",FACE,{"disambiguationData":[OSD([subQ3,subQ2,subQ1,subQ0])],"isStart":false}),makeQuery(id+"F26.opExtrude","CAP_FACE",FACE,{"disambiguationData":[OSD([subQ3,subQ2,subQ1,subQ0])],"isStart":false})]});}
            var Q2;
            Q2=makeQuery(id+"F18.opExtrude","CAP_FACE",FACE,{"disambiguationData":[OSD([sQuery(id+"F17.wireOp",EDGE,"E56.right"),sQuery(id+"F17.wireOp",EDGE,"E57"),sQuery(id+"F17.wireOp",EDGE,"E58"),sQuery(id+"F17.wireOp",EDGE,"E66"),sQuery(id+"F17.wireOp",EDGE,"E67"),sQuery(id+"F17.wireOp",EDGE,"E86.top")])],"isStart":false});
            extrude(context, id + "F49", {"entities" : qUnion([Q0, Q1, Q2]), "depth" : 25.4 * mm});
        }
        {
            var Q0;
            Q0=qCreatedBy(makeId("Top.planeOp"),FACE);
            var sketch = newSketch(context, id + "F50", { "sketchPlane" : qUnion([Q0])});
            skLineSegment(sketch, "E147.bottom", {"start": v(6464.3, -120.65) * mm, "end": v(7073.9, -120.65) * mm});
            skLineSegment(sketch, "E147.top", {"start": v(6464.3, -781.05) * mm, "end": v(7073.9, -781.05) * mm});
            skLineSegment(sketch, "E147.left", {"start": v(6464.3, -120.65) * mm, "end": v(6464.3, -781.05) * mm});
            skLineSegment(sketch, "E147.right", {"start": v(7073.9, -120.65) * mm, "end": v(7073.9, -781.05) * mm});
            skSolve(sketch);
        }
        {
            var Q0;
            Q0=makeQuery(id+"F50.imprint","IMPRINT",FACE,{"disambiguationData":[TD([[makeQuery(id+"F50.imprint","IMPRINT",EDGE,{"derivedFrom":sQuery(id+"F50.wireOp",EDGE,"E147.bottom")}),-1.0]])]});
            extrude(context, id + "F51", {"entities" : qUnion([Q0]), "depth" : 838.2 * mm});
        }
    });
